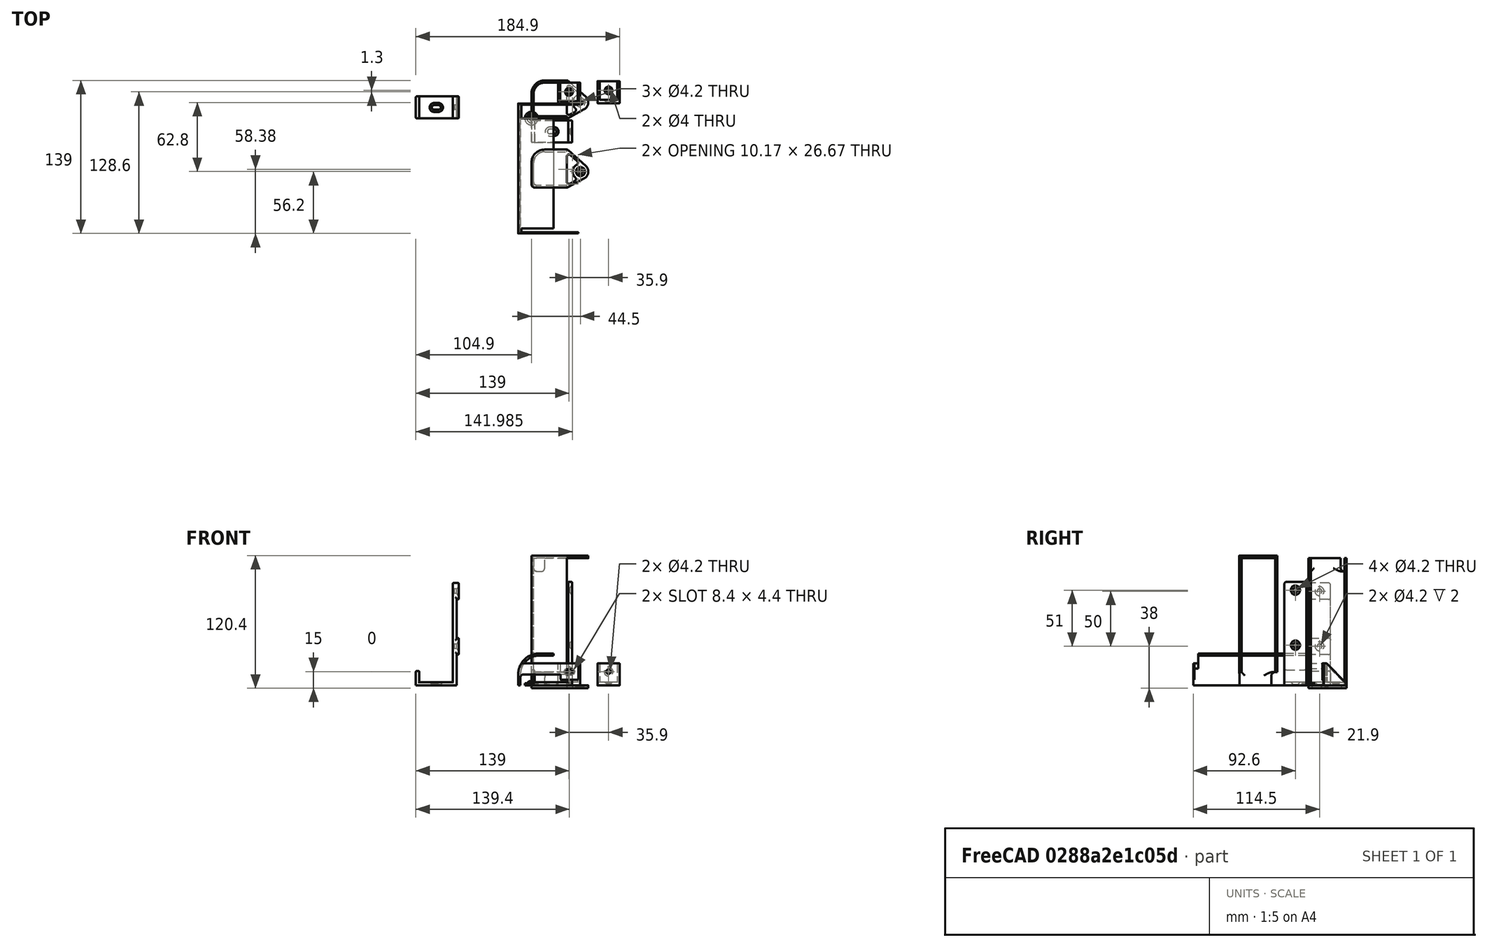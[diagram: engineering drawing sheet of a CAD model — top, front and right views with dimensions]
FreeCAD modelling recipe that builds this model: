
FCSTD DOCUMENT  (FreeCAD 1.0R39285 (Git))
Label: Mounts
License: All rights reserved
LicenseURL: https://en.wikipedia.org/wiki/All_rights_reserved
objects: Sketcher::SketchObject×38, PartDesign::Pad×19, PartDesign::Hole×10, PartDesign::Pocket×8, PartDesign::Body×8, Mesh::Feature×8, PartDesign::Fillet×3, PartDesign::Chamfer×2, PartDesign::Plane×1, PartDesign::Revolution×1
note: 214 computed .brp shape members not serialized (recipe doc carries the construction recipe); baked Part::Feature solids carry a one-line shape summary decoded from their .brp

FEATURE [Sketcher::SketchObject] Sketch  label="Sk-Mounting Angle Base"
  ArcFitTolerance = 1e-06
  AttachmentSupport = -> [XZ_Plane]
  FullyConstrained = true
  MakeInternals = false
  MapMode = 5
  Placement = pos=(0,0,0) rot=(1,0,0;1.5708rad)
  sketch-geometry (19):
    g0: LineSegment StartX=0 StartY=19 StartZ=0 EndX=0 EndY=1 EndZ=0
    g1: LineSegment StartX=1 StartY=0 StartZ=0 EndX=19 EndY=0 EndZ=0
    g2: LineSegment StartX=20 StartY=1 StartZ=0 EndX=20 EndY=2 EndZ=0
    g3: LineSegment StartX=19.7071 StartY=2.70711 StartZ=0 EndX=2.70711 EndY=19.7071 EndZ=0
    g4: LineSegment StartX=2 StartY=20 StartZ=0 EndX=1 EndY=20 EndZ=0
    g5: ArcOfCircle CenterX=1 CenterY=19 CenterZ=0 NormalX=0 NormalY=0 NormalZ=1 AngleXU=0 Radius=1 StartAngle=1.5708 EndAngle=3.14159
    g6: GeomPoint [constr] X=0 Y=20 Z=0
    g7: ArcOfCircle CenterX=2 CenterY=19 CenterZ=0 NormalX=0 NormalY=0 NormalZ=1 AngleXU=0 Radius=1 StartAngle=0.785398 EndAngle=1.5708
    g8: GeomPoint [constr] X=2.41421 Y=20 Z=0
    g9: ArcOfCircle CenterX=19 CenterY=2 CenterZ=0 NormalX=0 NormalY=0 NormalZ=1 AngleXU=0 Radius=1 StartAngle=1e-16 EndAngle=0.785398
    g10: GeomPoint [constr] X=20 Y=2.41421 Z=0
    g11: ArcOfCircle CenterX=19 CenterY=1 CenterZ=0 NormalX=0 NormalY=0 NormalZ=1 AngleXU=0 Radius=1 StartAngle=4.71239 EndAngle=6.28319
    g12: GeomPoint [constr] X=20 Y=0 Z=0
    g13: ArcOfCircle CenterX=1 CenterY=1 CenterZ=0 NormalX=0 NormalY=0 NormalZ=1 AngleXU=0 Radius=1 StartAngle=3.14159 EndAngle=4.71239
    g14: GeomPoint [constr] X=0 Y=0 Z=0
    g15: ArcOfCircle [constr] CenterX=2 CenterY=19 CenterZ=0 NormalX=0 NormalY=0 NormalZ=1 AngleXU=0 Radius=1 StartAngle=-1.8e-15 EndAngle=1.5708
    g16: LineSegment [constr] StartX=2 StartY=19 StartZ=0 EndX=3 EndY=19 EndZ=0
    g17: ArcOfCircle [constr] CenterX=19 CenterY=2 CenterZ=0 NormalX=0 NormalY=0 NormalZ=1 AngleXU=0 Radius=1 StartAngle=0 EndAngle=1.5708
    g18: LineSegment [constr] StartX=19 StartY=3 StartZ=0 EndX=19 EndY=2 EndZ=0
  constraints (44):
    c: Coincident(g14,g-1)
    c: Horizontal(g1)
    c: Vertical(g2)
    c: Vertical(g0)
    c: Horizontal(g4)
    c: DistanceY(g14,g6) = 20
    c: DistanceX(g14,g12) = 20
    c: PointOnObject(g6,g0)
    c: PointOnObject(g6,g4)
    c: Tangent(g0,g5) = -1.5708
    c: Tangent(g4,g5) = -1.5708
    c: PointOnObject(g8,g4)
    c: PointOnObject(g8,g3)
    c: Tangent(g4,g7) = -1.5708
    c: Tangent(g3,g7) = -1.5708
    c: PointOnObject(g10,g3)
    c: PointOnObject(g10,g2)
    c: Tangent(g3,g9) = -1.5708
    c: Tangent(g2,g9) = -1.5708
    c: PointOnObject(g12,g2)
    c: PointOnObject(g12,g1)
    c: Tangent(g2,g11) = -1.5708
    c: Tangent(g1,g11) = -1.5708
    c: PointOnObject(g14,g1)
    c: PointOnObject(g14,g0)
    c: Tangent(g1,g13) = -1.5708
    c: Tangent(g0,g13) = -1.5708
    c: Equal(g5,g7)
    c: Equal(g7,g9)
    c: Equal(g9,g11)
    c: Equal(g11,g13)
    c: Radius(g5) = 1
    c: Equal(g4,g2)
    c: Coincident(g15,g7)
    c: Coincident(g15,g4)
    c: Coincident(g16,g7)
    c: Coincident(g16,g15)
    c: Horizontal(g16)
    c: DistanceX(g0,g15) = 3
    c: Coincident(g17,g9)
    c: Coincident(g17,g2)
    c: Coincident(g18,g17)
    c: Coincident(g18,g9)
    c: Vertical(g18)
FEATURE [PartDesign::Pad] Pad  label="P-Mounting Angle Base"
  Direction = (0,-1,2e-16)
  Length = 20
  Length2 = 10
  Placement = pos=(0,0,0) rot=(1,0,0;1.5708rad)
  Profile = -> Sketch
  ReferenceAxis = -> Sketch [N_Axis]
  Refine = true
  Suppressed = false
  Type = 0
FEATURE [Sketcher::SketchObject] Sketch001  label="Sk-Mounting Angle Pocket"
  ArcFitTolerance = 1e-06
  AttachmentOffset = pos=(0,0,-2) rot=(0,0,1;0rad)
  AttachmentSupport = -> [Pad]
  ExternalGeometry = -> [Pad]
  FullyConstrained = true
  MakeInternals = false
  MapMode = 5
  Placement = pos=(0,-18,-4e-16) rot=(1,0,0;1.5708rad)
  sketch-geometry (20):
    g0: LineSegment StartX=3 StartY=19 StartZ=0 EndX=3 EndY=4 EndZ=0
    g1: LineSegment StartX=4 StartY=3 StartZ=0 EndX=19 EndY=3 EndZ=0
    g2: ArcOfCircle CenterX=4 CenterY=4 CenterZ=0 NormalX=0 NormalY=0 NormalZ=1 AngleXU=0 Radius=1 StartAngle=3.14159 EndAngle=4.71239
    g3: GeomPoint [constr] X=3 Y=3 Z=0
    g4: LineSegment [constr] StartX=2.7e-15 StartY=19 StartZ=0 EndX=2.7e-15 EndY=1 EndZ=0
    g5: LineSegment [constr] StartX=1 StartY=20 StartZ=0 EndX=2 EndY=20 EndZ=0
    g6: LineSegment [constr] StartX=1 StartY=2.75e-14 StartZ=0 EndX=19 EndY=2.75e-14 EndZ=0
    g7: LineSegment [constr] StartX=20 StartY=1 StartZ=0 EndX=20 EndY=2 EndZ=0
    g8: ArcOfCircle [constr] CenterX=1 CenterY=19 CenterZ=0 NormalX=0 NormalY=0 NormalZ=1 AngleXU=0 Radius=1 StartAngle=1.5708 EndAngle=3.14159
    g9: GeomPoint [constr] X=0 Y=20 Z=0
    g10: ArcOfCircle CenterX=2 CenterY=19 CenterZ=0 NormalX=0 NormalY=0 NormalZ=1 AngleXU=0 Radius=1 StartAngle=-3.189e-13 EndAngle=1.5708
    g11: GeomPoint [constr] X=3 Y=20 Z=0
    g12: ArcOfCircle [constr] CenterX=1 CenterY=1 CenterZ=0 NormalX=0 NormalY=0 NormalZ=1 AngleXU=0 Radius=1 StartAngle=3.14159 EndAngle=4.71239
    g13: GeomPoint [constr] X=0 Y=4.4e-15 Z=0
    g14: ArcOfCircle CenterX=19 CenterY=2 CenterZ=0 NormalX=0 NormalY=0 NormalZ=1 AngleXU=0 Radius=1 StartAngle=-1.643e-13 EndAngle=1.5708
    g15: GeomPoint [constr] X=20 Y=3 Z=0
    g16: ArcOfCircle [constr] CenterX=19 CenterY=1 CenterZ=0 NormalX=0 NormalY=0 NormalZ=1 AngleXU=0 Radius=1 StartAngle=4.71239 EndAngle=6.28319
    g17: GeomPoint [constr] X=20 Y=4.4e-15 Z=0
    g18: LineSegment StartX=2 StartY=20 StartZ=0 EndX=20 EndY=20 EndZ=0
    g19: LineSegment StartX=20 StartY=20 StartZ=0 EndX=20 EndY=2 EndZ=0
  constraints (43):
    c: Vertical(g0)
    c: Horizontal(g1)
    c: PointOnObject(g3,g0)
    c: PointOnObject(g3,g1)
    c: Tangent(g0,g2) = -1.5708
    c: Tangent(g1,g2) = -1.5708
    c: Horizontal(g5)
    c: Vertical(g4)
    c: Horizontal(g6)
    c: Vertical(g7)
    c: PointOnObject(g9,g4)
    c: PointOnObject(g9,g5)
    c: Tangent(g4,g8) = -1.5708
    c: Tangent(g5,g8) = 1.5708
    c: PointOnObject(g11,g5)
    c: PointOnObject(g11,g0)
    c: Tangent(g5,g10) = 1.5708
    c: Tangent(g0,g10) = 1.5708
    c: PointOnObject(g13,g4)
    c: PointOnObject(g13,g6)
    c: Tangent(g4,g12) = -1.5708
    c: Tangent(g6,g12) = -1.5708
    c: PointOnObject(g15,g1)
    c: PointOnObject(g15,g7)
    c: Tangent(g1,g14) = 1.5708
    c: Tangent(g7,g14) = -1.5708
    c: PointOnObject(g17,g6)
    c: PointOnObject(g17,g7)
    c: Tangent(g6,g16) = -1.5708
    c: Tangent(g7,g16) = -1.5708
    c: Equal(g10,g2)
    c: Equal(g2,g14)
    c: Equal(g16,g12)
    c: Equal(g8,g-4)
    c: Coincident(g4,g-4)
    c: Coincident(g10,g-3)
    c: Coincident(g6,g-5)
    c: Coincident(g14,g-6)
    c: Coincident(g18,g5)
    c: Horizontal(g18)
    c: Coincident(g19,g18)
    c: Coincident(g19,g7)
    c: Vertical(g19)
FEATURE [PartDesign::Pocket] Pocket  label="P- Mounting Angle Shape"
  BaseFeature = -> Pad
  Direction = (0,1,-2e-16)
  Length = 16
  Length2 = 5
  Placement = pos=(0,0,0) rot=(1,0,0;1.5708rad)
  Profile = -> Sketch001
  ReferenceAxis = -> Sketch001 [N_Axis]
  Refine = true
  Suppressed = false
  Type = 0
FEATURE [Sketcher::SketchObject] Sketch002  label="Sk-Mounting Angle Screwhole Bottom"
  ArcFitTolerance = 1e-06
  AttachmentSupport = -> [Pocket]
  ExternalGeometry = -> [Pocket]
  FullyConstrained = true
  MakeInternals = false
  MapMode = 5
  Placement = pos=(0,1.3e-15,3) rot=(0,0,1;3.14159rad)
  sketch-geometry (2):
    g0: Circle CenterX=-11.5 CenterY=10 CenterZ=0 NormalX=0 NormalY=0 NormalZ=1 AngleXU=0 Radius=2
    g1: LineSegment [constr] StartX=-4 StartY=10 StartZ=0 EndX=-19 EndY=10 EndZ=0
  constraints (4):
    c: Diameter(g0) = 4
    c: Symmetric(g-4,g-4,g1)
    c: Symmetric(g-3,g-3,g1)
    c: Symmetric(g1,g1,g0)
FEATURE [PartDesign::Hole] Hole  label="P-Mounting Angle Screwhole Bottom"
  BaseFeature = -> Pocket
  CustomThreadClearance = 0
  Depth = 69.9749
  DepthType = 1
  Diameter = 4
  DrillForDepth = false
  DrillPoint = 1
  DrillPointAngle = 118
  HoleCutCountersinkAngle = 90
  HoleCutCustomValues = false
  HoleCutDepth = 0
  HoleCutDiameter = 7
  HoleCutType = 2
  ModelThread = false
  Placement = pos=(0,0,0) rot=(1,0,0;1.5708rad)
  Profile = -> Sketch002
  Refine = true
  Suppressed = false
  Tapered = false
  TaperedAngle = 90
  ThreadClass = 0
  ThreadDepth = 69.9749
  ThreadDepthType = 0
  ThreadDirection = 0
  ThreadFit = 0
  ThreadSize = 0
  ThreadType = 0
  Threaded = false
  UseCustomThreadClearance = false
FEATURE [Sketcher::SketchObject] Sketch003  label="Sk-Mounting Angle Screwhole Side"
  ArcFitTolerance = 1e-06
  AttachmentSupport = -> [Hole]
  ExternalGeometry = -> [Hole]
  FullyConstrained = true
  MakeInternals = false
  MapMode = 5
  Placement = pos=(3,0,0) rot=(0.707107,0,0.707107;3.14159rad)
  sketch-geometry (2):
    g0: LineSegment [constr] StartX=1.8e-15 StartY=10 StartZ=0 EndX=12.5 EndY=10 EndZ=0
    g1: Circle CenterX=12.5 CenterY=10 CenterZ=0 NormalX=0 NormalY=0 NormalZ=1 AngleXU=0 Radius=2.2
  constraints (5):
    c: Symmetric(g-3,g-3,g0)
    c: Horizontal(g0)
    c: DistanceX(g0,g0) = 12.5
    c: Diameter(g1) = 4.4
    c: Coincident(g1,g0)
FEATURE [PartDesign::Hole] Hole001  label="P-Mounting Angle complete"
  BaseFeature = -> Hole
  CustomThreadClearance = 0
  Depth = 25
  DepthType = 0
  Diameter = 4.2
  DrillForDepth = false
  DrillPoint = 1
  DrillPointAngle = 118
  HoleCutCountersinkAngle = 90
  HoleCutCustomValues = false
  HoleCutDepth = 0
  HoleCutDiameter = 8.1
  HoleCutType = 2
  ModelThread = false
  Placement = pos=(0,0,0) rot=(1,0,0;1.5708rad)
  Profile = -> Sketch003
  Refine = true
  Suppressed = false
  Tapered = false
  TaperedAngle = 90
  ThreadClass = 0
  ThreadDepth = 25
  ThreadDepthType = 0
  ThreadDirection = 0
  ThreadFit = 0
  ThreadSize = 0
  ThreadType = 0
  Threaded = false
  UseCustomThreadClearance = false
FEATURE [PartDesign::Body] Body  label="B-Power Supply Mounting Angle - Flat"
  AllowCompound = false
  Group = -> [Sketch,Pad,Sketch001,Pocket,Sketch002,Hole,Sketch003,Hole001]
  Origin = -> Origin
  Placement = pos=(60,13.9,0) rot=(0,0,1;1.5708rad)
  Tip = -> Hole001
FEATURE [Sketcher::SketchObject] Sketch004  label="Sk-Mounting Angle Bracket Base"
  ArcFitTolerance = 1e-06
  AttachmentSupport = -> [XZ_Plane001]
  FullyConstrained = true
  MakeInternals = false
  MapMode = 5
  Placement = pos=(0,0,0) rot=(1,0,0;1.5708rad)
  sketch-geometry (20):
    g0: LineSegment [constr] StartX=0 StartY=19 StartZ=0 EndX=0 EndY=1 EndZ=0
    g1: LineSegment StartX=1 StartY=0 StartZ=0 EndX=19 EndY=0 EndZ=0
    g2: LineSegment StartX=20 StartY=1 StartZ=0 EndX=20 EndY=2 EndZ=0
    g3: LineSegment StartX=19.7071 StartY=2.70711 StartZ=0 EndX=2.70711 EndY=19.7071 EndZ=0
    g4: LineSegment StartX=2 StartY=20 StartZ=0 EndX=1 EndY=20 EndZ=0
    g5: ArcOfCircle [constr] CenterX=1 CenterY=19 CenterZ=0 NormalX=0 NormalY=0 NormalZ=1 AngleXU=0 Radius=1 StartAngle=1.5708 EndAngle=3.14159
    g6: GeomPoint [constr] X=0 Y=20 Z=0
    g7: ArcOfCircle CenterX=2 CenterY=19 CenterZ=0 NormalX=0 NormalY=0 NormalZ=1 AngleXU=0 Radius=1 StartAngle=0.785398 EndAngle=1.5708
    g8: GeomPoint [constr] X=2.41421 Y=20 Z=0
    g9: ArcOfCircle CenterX=19 CenterY=2 CenterZ=0 NormalX=0 NormalY=0 NormalZ=1 AngleXU=0 Radius=1 StartAngle=1e-16 EndAngle=0.785398
    g10: GeomPoint [constr] X=20 Y=2.41421 Z=0
    g11: ArcOfCircle CenterX=19 CenterY=1 CenterZ=0 NormalX=0 NormalY=0 NormalZ=1 AngleXU=0 Radius=1 StartAngle=4.71239 EndAngle=6.28319
    g12: GeomPoint [constr] X=20 Y=0 Z=0
    g13: ArcOfCircle [constr] CenterX=1 CenterY=1 CenterZ=0 NormalX=0 NormalY=0 NormalZ=1 AngleXU=0 Radius=1 StartAngle=3.14159 EndAngle=4.71239
    g14: GeomPoint [constr] X=0 Y=0 Z=0
    g15: ArcOfCircle [constr] CenterX=2 CenterY=19 CenterZ=0 NormalX=0 NormalY=0 NormalZ=1 AngleXU=0 Radius=1 StartAngle=-1.8e-15 EndAngle=1.5708
    g16: LineSegment [constr] StartX=2 StartY=19 StartZ=0 EndX=3 EndY=19 EndZ=0
    g17: ArcOfCircle [constr] CenterX=19 CenterY=2 CenterZ=0 NormalX=0 NormalY=0 NormalZ=1 AngleXU=0 Radius=1 StartAngle=0 EndAngle=1.5708
    g18: LineSegment [constr] StartX=19 StartY=3 StartZ=0 EndX=19 EndY=2 EndZ=0
    g19: LineSegment StartX=1 StartY=20 StartZ=0 EndX=1 EndY=0 EndZ=0
  constraints (46):
    c: Coincident(g14,g-1)
    c: Horizontal(g1)
    c: Vertical(g2)
    c: Vertical(g0)
    c: Horizontal(g4)
    c: DistanceY(g14,g6) = 20
    c: DistanceX(g14,g12) = 20
    c: PointOnObject(g6,g0)
    c: PointOnObject(g6,g4)
    c: Tangent(g0,g5) = -1.5708
    c: Tangent(g4,g5) = -1.5708
    c: PointOnObject(g8,g4)
    c: PointOnObject(g8,g3)
    c: Tangent(g4,g7) = -1.5708
    c: Tangent(g3,g7) = -1.5708
    c: PointOnObject(g10,g3)
    c: PointOnObject(g10,g2)
    c: Tangent(g3,g9) = -1.5708
    c: Tangent(g2,g9) = -1.5708
    c: PointOnObject(g12,g2)
    c: PointOnObject(g12,g1)
    c: Tangent(g2,g11) = -1.5708
    c: Tangent(g1,g11) = -1.5708
    c: PointOnObject(g14,g1)
    c: PointOnObject(g14,g0)
    c: Tangent(g1,g13) = -1.5708
    c: Tangent(g0,g13) = -1.5708
    c: Equal(g5,g7)
    c: Equal(g7,g9)
    c: Equal(g9,g11)
    c: Equal(g11,g13)
    c: Radius(g5) = 1
    c: Equal(g4,g2)
    c: Coincident(g15,g7)
    c: Coincident(g15,g4)
    c: Coincident(g16,g7)
    c: Coincident(g16,g15)
    c: Horizontal(g16)
    c: DistanceX(g0,g15) = 3
    c: Coincident(g17,g9)
    c: Coincident(g17,g2)
    c: Coincident(g18,g17)
    c: Coincident(g18,g9)
    c: Vertical(g18)
    c: Coincident(g19,g4)
    c: Coincident(g19,g1)
FEATURE [PartDesign::Pad] Pad001  label="P-Mounting Angle Bracket Base"
  Direction = (0,-1,2e-16)
  Length = 20
  Length2 = 10
  Placement = pos=(0,0,0) rot=(1,0,0;1.5708rad)
  Profile = -> Sketch004
  ReferenceAxis = -> Sketch004 [N_Axis]
  Refine = true
  Suppressed = false
  Type = 0
FEATURE [Sketcher::SketchObject] Sketch005  label="Sk-Mounting Angle Bracket Pocket"
  ArcFitTolerance = 1e-06
  AttachmentOffset = pos=(0,0,-2) rot=(0,0,1;0rad)
  AttachmentSupport = -> [Pad001]
  ExternalGeometry = -> [Pad001]
  FullyConstrained = true
  MakeInternals = false
  MapMode = 5
  Placement = pos=(0,-18,-4e-16) rot=(1,0,0;1.5708rad)
  sketch-geometry (8):
    g0: LineSegment StartX=3 StartY=19 StartZ=0 EndX=3 EndY=4 EndZ=0
    g1: LineSegment StartX=4 StartY=3 StartZ=0 EndX=19 EndY=3 EndZ=0
    g2: ArcOfCircle CenterX=4 CenterY=4 CenterZ=0 NormalX=0 NormalY=0 NormalZ=1 AngleXU=0 Radius=1 StartAngle=3.14159 EndAngle=4.71239
    g3: GeomPoint [constr] X=3 Y=3 Z=0
    g4: ArcOfCircle CenterX=2 CenterY=19 CenterZ=0 NormalX=0 NormalY=0 NormalZ=1 AngleXU=0 Radius=1 StartAngle=1.5e-15 EndAngle=1.5708
    g5: ArcOfCircle CenterX=19 CenterY=2 CenterZ=0 NormalX=0 NormalY=0 NormalZ=1 AngleXU=0 Radius=1 StartAngle=0 EndAngle=1.5708
    g6: LineSegment StartX=2 StartY=20 StartZ=0 EndX=20 EndY=20 EndZ=0
    g7: LineSegment StartX=20 StartY=20 StartZ=0 EndX=20 EndY=2 EndZ=0
  constraints (18):
    c: Vertical(g0)
    c: Horizontal(g1)
    c: PointOnObject(g3,g0)
    c: PointOnObject(g3,g1)
    c: Tangent(g0,g2) = -1.5708
    c: Tangent(g1,g2) = -1.5708
    c: Tangent(g0,g4) = 1.5708
    c: Tangent(g1,g5) = 1.5708
    c: Equal(g4,g2)
    c: Equal(g2,g5)
    c: Horizontal(g6)
    c: Coincident(g7,g6)
    c: Vertical(g7)
    c: Coincident(g5,g-4)
    c: PointOnObject(g-4,g5)
    c: Tangent(g7,g5) = 1.5708
    c: Tangent(g6,g4) = 1.5708
    c: Coincident(g4,g-3)
FEATURE [PartDesign::Pocket] Pocket001  label="P- Mounting Angle Bracket Shape"
  BaseFeature = -> Pad001
  Direction = (0,1,-2e-16)
  Length = 16
  Length2 = 5
  Placement = pos=(0,0,0) rot=(1,0,0;1.5708rad)
  Profile = -> Sketch005
  ReferenceAxis = -> Sketch005 [N_Axis]
  Refine = true
  Suppressed = false
  Type = 0
FEATURE [Sketcher::SketchObject] Sketch006  label="Sk-Mounting Angle Bracket Screwhole Bottom"
  ArcFitTolerance = 1e-06
  AttachmentSupport = -> [Pocket001]
  FullyConstrained = true
  MakeInternals = false
  MapMode = 5
  Placement = pos=(0,1.3e-15,3) rot=(0,0,1;3.14159rad)
  sketch-geometry (2):
    g0: Circle CenterX=-11.5 CenterY=10 CenterZ=0 NormalX=0 NormalY=0 NormalZ=1 AngleXU=0 Radius=2
    g1: LineSegment [constr] StartX=-4 StartY=10 StartZ=0 EndX=-19 EndY=10 EndZ=0
  constraints (4):
    c: Diameter(g0) = 4
    c: Symmetric(g-4,g-4,g1)
    c: Symmetric(g-3,g-3,g1)
    c: Symmetric(g1,g1,g0)
FEATURE [PartDesign::Hole] Hole002  label="P-Mounting Angle Bracket Screwhole Bottom"
  BaseFeature = -> Pocket001
  CustomThreadClearance = 0
  Depth = 69.9749
  DepthType = 1
  Diameter = 4
  DrillForDepth = false
  DrillPoint = 1
  DrillPointAngle = 118
  HoleCutCountersinkAngle = 90
  HoleCutCustomValues = false
  HoleCutDepth = 0
  HoleCutDiameter = 7
  HoleCutType = 2
  ModelThread = false
  Placement = pos=(0,0,0) rot=(1,0,0;1.5708rad)
  Profile = -> Sketch006
  Refine = true
  Suppressed = false
  Tapered = false
  TaperedAngle = 90
  ThreadClass = 0
  ThreadDepth = 69.9749
  ThreadDepthType = 0
  ThreadDirection = 0
  ThreadFit = 0
  ThreadSize = 0
  ThreadType = 0
  Threaded = false
  UseCustomThreadClearance = false
FEATURE [Sketcher::SketchObject] Sketch007  label="Sk-Mounting Angle Bracket Screwhole Side"
  ArcFitTolerance = 1e-06
  AttachmentSupport = -> [Hole002]
  ExternalGeometry = -> [Hole002]
  FullyConstrained = true
  MakeInternals = false
  MapMode = 5
  Placement = pos=(3,0,0) rot=(0.707107,0,0.707107;3.14159rad)
  sketch-geometry (2):
    g0: LineSegment [constr] StartX=5.8e-15 StartY=10 StartZ=0 EndX=12.5 EndY=10 EndZ=0
    g1: Circle CenterX=12.5 CenterY=10 CenterZ=0 NormalX=0 NormalY=0 NormalZ=1 AngleXU=0 Radius=2.2
  constraints (5):
    c: Horizontal(g0)
    c: DistanceX(g0,g0) = 12.5
    c: Diameter(g1) = 4.4
    c: Coincident(g1,g0)
    c: Symmetric(g-3,g-3,g0)
FEATURE [PartDesign::Hole] Hole003  label="P-Mounting Angle Bracket complete"
  BaseFeature = -> Hole002
  CustomThreadClearance = 0
  Depth = 25
  DepthType = 0
  Diameter = 4.2
  DrillForDepth = false
  DrillPoint = 1
  DrillPointAngle = 118
  HoleCutCountersinkAngle = 90
  HoleCutCustomValues = false
  HoleCutDepth = 0
  HoleCutDiameter = 8.1
  HoleCutType = 2
  ModelThread = false
  Placement = pos=(0,0,0) rot=(1,0,0;1.5708rad)
  Profile = -> Sketch007
  Refine = true
  Suppressed = false
  Tapered = false
  TaperedAngle = 90
  ThreadClass = 0
  ThreadDepth = 25
  ThreadDepthType = 0
  ThreadDirection = 0
  ThreadFit = 0
  ThreadSize = 0
  ThreadType = 0
  Threaded = false
  UseCustomThreadClearance = false
FEATURE [PartDesign::Body] Body001  label="B-Power Supply Mounting Angle for Bracket - Flat"
  AllowCompound = false
  Group = -> [Sketch004,Pad001,Sketch005,Pocket001,Sketch006,Hole002,Sketch007,Hole003]
  Origin = -> Origin001
  Placement = pos=(24.1,12.6,0) rot=(0,0,1;1.5708rad)
  Tip = -> Hole003
FEATURE [Sketcher::SketchObject] Sketch008  label="Sk-Bracket Shield"
  ArcFitTolerance = 1e-06
  AttachmentSupport = -> [XZ_Plane002]
  FullyConstrained = true
  MakeInternals = false
  MapMode = 5
  Placement = pos=(0,0,0) rot=(1,0,0;1.5708rad)
  sketch-geometry (11):
    g0: LineSegment StartX=20 StartY=29 StartZ=0 EndX=7 EndY=29 EndZ=0
    g1: LineSegment StartX=-12 StartY=10 StartZ=0 EndX=-12 EndY=0 EndZ=0
    g2: LineSegment StartX=-12 StartY=0 StartZ=0 EndX=-10 EndY=0 EndZ=0
    g3: LineSegment StartX=-10 StartY=0 StartZ=0 EndX=-10 EndY=10 EndZ=0
    g4: LineSegment StartX=7 StartY=27 StartZ=0 EndX=20 EndY=27 EndZ=0
    g5: LineSegment StartX=20 StartY=27 StartZ=0 EndX=20 EndY=29 EndZ=0
    g6: ArcOfCircle CenterX=7 CenterY=10 CenterZ=0 NormalX=0 NormalY=0 NormalZ=1 AngleXU=0 Radius=19 StartAngle=1.5708 EndAngle=3.14159
    g7: GeomPoint [constr] X=-12 Y=29 Z=0
    g8: ArcOfCircle CenterX=7 CenterY=10 CenterZ=0 NormalX=0 NormalY=0 NormalZ=1 AngleXU=0 Radius=17 StartAngle=1.5708 EndAngle=3.14159
    g9: GeomPoint [constr] X=-10 Y=27 Z=0
    g10: LineSegment [constr] StartX=-10 StartY=0 StartZ=0 EndX=0 EndY=0 EndZ=0
  constraints (28):
    c: Horizontal(g0)
    c: Coincident(g1,g2)
    c: Horizontal(g2)
    c: Coincident(g2,g3)
    c: Horizontal(g4)
    c: Coincident(g4,g5)
    c: Coincident(g5,g0)
    c: Vertical(g5)
    c: Vertical(g1)
    c: Vertical(g3)
    c: PointOnObject(g7,g0)
    c: PointOnObject(g7,g1)
    c: Tangent(g0,g6) = -1.5708
    c: Tangent(g1,g6) = -1.5708
    c: PointOnObject(g9,g4)
    c: PointOnObject(g9,g3)
    c: Tangent(g4,g8) = 1.5708
    c: Tangent(g3,g8) = 1.5708
    c: Coincident(g10,g2)
    c: Coincident(g10,g-1)
    c: Horizontal(g10)
    c: DistanceX(g10,g10) = 10
    c: DistanceX(g2,g2) = 2
    c: Coincident(g6,g8)
    c: DistanceY(g1,g0) = 29
    c: DistanceX(g10,g4) = 20
    c: Radius(g8) = 17
    c: DistanceY(g1,g1) = 10
FEATURE [PartDesign::Pad] Pad002  label="P-Bracket Shield"
  Direction = (0,-1,2e-16)
  Length = 100
  Length2 = 10
  Placement = pos=(0,0,0) rot=(1,0,0;1.5708rad)
  Profile = -> Sketch008
  ReferenceAxis = -> Sketch008 [N_Axis]
  Refine = true
  Suppressed = false
  Type = 0
FEATURE [Sketcher::SketchObject] Sketch009  label="Sk-Bracket Dist front"
  ArcFitTolerance = 1e-06
  AttachmentSupport = -> [Pad002]
  ExternalGeometry = -> [Pad002]
  FullyConstrained = true
  MakeInternals = false
  MapMode = 5
  Placement = pos=(0,-100,0) rot=(1,0,0;1.5708rad)
  sketch-geometry (6):
    g0: ArcOfCircle CenterX=7 CenterY=10 CenterZ=0 NormalX=0 NormalY=0 NormalZ=1 AngleXU=0 Radius=17 StartAngle=2.82507 EndAngle=3.14159
    g1: ArcOfCircle CenterX=7 CenterY=10 CenterZ=0 NormalX=0 NormalY=0 NormalZ=1 AngleXU=0 Radius=19 StartAngle=2.58733 EndAngle=3.14159
    g2: LineSegment StartX=-9.15549 StartY=20 StartZ=0 EndX=-9.15549 EndY=15.2915 EndZ=0
    g3: LineSegment StartX=-10 StartY=10 StartZ=0 EndX=-10 EndY=2.31e-14 EndZ=0
    g4: LineSegment StartX=-10 StartY=2.31e-14 StartZ=0 EndX=-12 EndY=2.22e-14 EndZ=0
    g5: LineSegment StartX=-12 StartY=2.22e-14 StartZ=0 EndX=-12 EndY=10 EndZ=0
  constraints (15):
    c: Coincident(g0,g-3)
    c: Coincident(g1,g0)
    c: Coincident(g2,g1)
    c: Coincident(g2,g0)
    c: Vertical(g2)
    c: Tangent(g3,g0) = -1.5708
    c: Coincident(g3,g-4)
    c: Coincident(g4,g3)
    c: Coincident(g4,g-4)
    c: Coincident(g5,g4)
    c: Coincident(g5,g1)
    c: Vertical(g5)
    c: PointOnObject(g0,g-3)
    c: Equal(g3,g5)
    c: DistanceY(g4,g1) = 20
FEATURE [PartDesign::Pad] Pad003  label="P-Bracket Shield left dist"
  BaseFeature = -> Pad002
  Direction = (0,-1,2e-16)
  Length = 3.5
  Length2 = 10
  Placement = pos=(0,0,0) rot=(1,0,0;1.5708rad)
  Profile = -> Sketch009
  ReferenceAxis = -> Sketch009 [N_Axis]
  Refine = true
  Suppressed = false
  Type = 0
FEATURE [Sketcher::SketchObject] Sketch010  label="Sk-Bracket Dist rear"
  ArcFitTolerance = 1e-06
  AttachmentSupport = -> [Pad003]
  ExternalGeometry = -> [Pad003]
  FullyConstrained = true
  MakeInternals = false
  MapMode = 5
  Placement = pos=(0,4.3e-15,0) rot=(-1,0,0;1.5708rad)
  sketch-geometry (6):
    g0: ArcOfCircle CenterX=7 CenterY=-10 CenterZ=0 NormalX=0 NormalY=0 NormalZ=1 AngleXU=0 Radius=17 StartAngle=3.14159 EndAngle=3.45812
    g1: ArcOfCircle CenterX=7 CenterY=-10 CenterZ=0 NormalX=0 NormalY=0 NormalZ=1 AngleXU=0 Radius=19 StartAngle=3.14159 EndAngle=3.69585
    g2: LineSegment StartX=-9.15549 StartY=-20 StartZ=0 EndX=-9.15549 EndY=-15.2915 EndZ=0
    g3: LineSegment StartX=-10 StartY=-10 StartZ=0 EndX=-10 EndY=0 EndZ=0
    g4: LineSegment StartX=-10 StartY=0 StartZ=0 EndX=-12 EndY=0 EndZ=0
    g5: LineSegment StartX=-12 StartY=0 StartZ=0 EndX=-12 EndY=-10 EndZ=0
  constraints (15):
    c: Coincident(g0,g-3)
    c: Coincident(g0,g-3)
    c: Coincident(g1,g0)
    c: Coincident(g2,g1)
    c: Coincident(g2,g0)
    c: Vertical(g2)
    c: Coincident(g3,g0)
    c: Coincident(g3,g-4)
    c: Coincident(g4,g3)
    c: Coincident(g4,g-4)
    c: Coincident(g5,g4)
    c: Coincident(g5,g1)
    c: Vertical(g5)
    c: PointOnObject(g0,g-5)
    c: Equal(g3,g5)
FEATURE [PartDesign::Pad] Pad004  label="P-Bracket Shield dists"
  BaseFeature = -> Pad003
  Direction = (0,1,2e-16)
  Length = 12.5
  Length2 = 10
  Placement = pos=(0,0,0) rot=(1,0,0;1.5708rad)
  Profile = -> Sketch010
  ReferenceAxis = -> Sketch010 [N_Axis]
  Refine = true
  Suppressed = false
  Type = 0
FEATURE [Sketcher::SketchObject] Sketch011  label="Sk-Bracket front mount"
  ArcFitTolerance = 1e-06
  AttachmentSupport = -> [Pad004]
  ExternalGeometry = -> [Pad004]
  FullyConstrained = true
  MakeInternals = false
  MapMode = 5
  Placement = pos=(0,-103.5,0) rot=(1,0,0;1.5708rad)
  sketch-geometry (33):
    g0: ArcOfCircle CenterX=7 CenterY=10 CenterZ=0 NormalX=0 NormalY=0 NormalZ=1 AngleXU=0 Radius=19 StartAngle=2.58733 EndAngle=3.14159
    g1: LineSegment StartX=-9.15549 StartY=20 StartZ=0 EndX=41.5 EndY=20 EndZ=0
    g2: LineSegment StartX=42.5 StartY=19 StartZ=0 EndX=42.5 EndY=6 EndZ=0
    g3: LineSegment StartX=26.5 StartY=6 StartZ=0 EndX=26.5 EndY=9 EndZ=0
    g4: LineSegment [constr] StartX=20 StartY=29 StartZ=0 EndX=2 EndY=29 EndZ=0
    g5: LineSegment [constr] StartX=2 StartY=29 StartZ=0 EndX=2 EndY=12.5 EndZ=0
    g6: LineSegment [constr] StartX=2 StartY=12.5 StartZ=0 EndX=2 EndY=0 EndZ=0
    g7: ArcOfCircle CenterX=32.5 CenterY=12.5 CenterZ=0 NormalX=0 NormalY=0 NormalZ=1 AngleXU=0 Radius=2.2 StartAngle=1.5708 EndAngle=4.71239
    g8: ArcOfCircle CenterX=36.5 CenterY=12.5 CenterZ=0 NormalX=0 NormalY=0 NormalZ=1 AngleXU=0 Radius=2.2 StartAngle=4.71239 EndAngle=7.85398
    g9: LineSegment StartX=32.5 StartY=14.7 StartZ=0 EndX=36.5 EndY=14.7 EndZ=0
    g10: LineSegment StartX=32.5 StartY=10.3 StartZ=0 EndX=36.5 EndY=10.3 EndZ=0
    g11: LineSegment [constr] StartX=2 StartY=12.5 StartZ=0 EndX=32.5 EndY=12.5 EndZ=0
    g12: LineSegment [constr] StartX=32.5 StartY=12.5 StartZ=0 EndX=34.5 EndY=12.5 EndZ=0
    g13: LineSegment [constr] StartX=34.5 StartY=12.5 StartZ=0 EndX=36.5 EndY=12.5 EndZ=0
    g14: LineSegment StartX=41.5 StartY=5 StartZ=0 EndX=34.5 EndY=5 EndZ=0
    g15: LineSegment StartX=34.5 StartY=5 StartZ=0 EndX=27.5 EndY=5 EndZ=0
    g16: LineSegment [constr] StartX=34.5 StartY=12.5 StartZ=0 EndX=34.5 EndY=5 EndZ=0
    g17: LineSegment [constr] StartX=34.5 StartY=12.5 StartZ=0 EndX=34.5 EndY=20 EndZ=0
    g18: LineSegment StartX=25.5 StartY=10 StartZ=0 EndX=-7 EndY=10 EndZ=0
    g19: LineSegment StartX=-12 StartY=10 StartZ=0 EndX=-12 EndY=0 EndZ=0
    g20: LineSegment StartX=-12 StartY=0 StartZ=0 EndX=-10 EndY=2.39e-14 EndZ=0
    g21: LineSegment StartX=-10 StartY=2.39e-14 StartZ=0 EndX=-10 EndY=7 EndZ=0
    g22: LineSegment [constr] StartX=-12 StartY=10 StartZ=0 EndX=-10 EndY=10 EndZ=0
    g23: ArcOfCircle CenterX=27.5 CenterY=6 CenterZ=0 NormalX=0 NormalY=0 NormalZ=1 AngleXU=0 Radius=1 StartAngle=3.14159 EndAngle=4.71239
    g24: GeomPoint [constr] X=26.5 Y=5 Z=0
    g25: ArcOfCircle CenterX=41.5 CenterY=6 CenterZ=0 NormalX=0 NormalY=0 NormalZ=1 AngleXU=0 Radius=1 StartAngle=4.71239 EndAngle=6.28319
    g26: GeomPoint [constr] X=42.5 Y=5 Z=0
    g27: ArcOfCircle CenterX=41.5 CenterY=19 CenterZ=0 NormalX=0 NormalY=0 NormalZ=1 AngleXU=0 Radius=1 StartAngle=0 EndAngle=1.5708
    g28: GeomPoint [constr] X=42.5 Y=20 Z=0
    g29: ArcOfCircle CenterX=25.5 CenterY=9 CenterZ=0 NormalX=0 NormalY=0 NormalZ=1 AngleXU=0 Radius=1 StartAngle=3e-16 EndAngle=1.5708
    g30: GeomPoint [constr] X=26.5 Y=10 Z=0
    g31: ArcOfCircle CenterX=-7 CenterY=7 CenterZ=0 NormalX=0 NormalY=0 NormalZ=1 AngleXU=0 Radius=3 StartAngle=1.5708 EndAngle=3.14159
    g32: GeomPoint [constr] X=-10 Y=10 Z=0
  constraints (80):
    c: Coincident(g0,g-3)
    c: Coincident(g0,g-3)
    c: Coincident(g1,g0)
    c: Horizontal(g1)
    c: Vertical(g2)
    c: Vertical(g3)
    c: PointOnObject(g-3,g1)
    c: Distance(g4) = 18
    c: Coincident(g4,g-4)
    c: Horizontal(g4)
    c: Coincident(g5,g4)
    c: Vertical(g5)
    c: Coincident(g11,g5)
    c: DistanceX(g11,g12) = 32.5
    c: Coincident(g6,g5)
    c: PointOnObject(g6,g-1)
    c: Vertical(g6)
    c: DistanceY(g6,g6) = 12.5
    c: Tangent(g7,g9) = 1.5708
    c: Tangent(g7,g10) = -1.5708
    c: Tangent(g8,g9) = 1.5708
    c: Tangent(g8,g10) = -1.5708
    c: Equal(g7,g8)
    c: Radius(g7) = 2.2
    c: Horizontal(g9)
    c: Coincident(g11,g12)
    c: Horizontal(g11)
    c: Horizontal(g12)
    c: Coincident(g11,g7)
    c: Coincident(g13,g12)
    c: Coincident(g13,g8)
    c: Equal(g13,g12)
    c: DistanceX(g10,g10) = 4
    c: Coincident(g14,g15)
    c: Horizontal(g14)
    c: Horizontal(g15)
    c: Coincident(g16,g12)
    c: Coincident(g16,g14)
    c: Vertical(g16)
    c: Coincident(g17,g12)
    c: PointOnObject(g17,g1)
    c: Vertical(g17)
    c: Equal(g17,g16)
    c: DistanceX(g24,g26) = 16
    c: Horizontal(g18)
    c: Coincident(g19,g0)
    c: Coincident(g19,g-5)
    c: Coincident(g20,g19)
    c: Coincident(g20,g-5)
    c: Coincident(g21,g20)
    c: Vertical(g21)
    c: Coincident(g22,g0)
    c: Coincident(g22,g32)
    c: Horizontal(g22)
    c: PointOnObject(g24,g3)
    c: PointOnObject(g24,g15)
    c: Tangent(g3,g23) = 1.5708
    c: Tangent(g15,g23) = 1.5708
    c: PointOnObject(g26,g2)
    c: PointOnObject(g26,g14)
    c: Tangent(g2,g25) = 1.5708
    c: Tangent(g14,g25) = 1.5708
    c: PointOnObject(g28,g1)
    c: PointOnObject(g28,g2)
    c: Tangent(g1,g27) = 1.5708
    c: Tangent(g2,g27) = 1.5708
    c: PointOnObject(g30,g18)
    c: PointOnObject(g30,g3)
    c: Tangent(g18,g29) = -1.5708
    c: Tangent(g3,g29) = -1.5708
    c: PointOnObject(g32,g21)
    c: PointOnObject(g32,g18)
    c: Tangent(g21,g31) = 1.5708
    c: Tangent(g18,g31) = -1.5708
    c: Equal(g29,g23)
    c: Equal(g23,g25)
    c: Equal(g25,g27)
    c: Radius(g27) = 1
    c: Radius(g31) = 3
    c: Equal(g15,g14)
FEATURE [PartDesign::Pad] Pad005  label="P-Bracket with front mount"
  BaseFeature = -> Pad004
  Direction = (0,-1,2e-16)
  Length = 1
  Length2 = 10
  Placement = pos=(0,0,0) rot=(1,0,0;1.5708rad)
  Profile = -> Sketch011
  ReferenceAxis = -> Sketch011 [N_Axis]
  Refine = true
  Suppressed = false
  Type = 0
FEATURE [Sketcher::SketchObject] Sketch012  label="Sk-Bracket rear mount"
  ArcFitTolerance = 1e-06
  AttachmentSupport = -> [Pad005]
  ExternalGeometry = -> [Pad005]
  FullyConstrained = false
  MakeInternals = false
  MapMode = 5
  Placement = pos=(0,12.5,2.8e-15) rot=(-1,0,0;1.5708rad)
  sketch-geometry (20):
    g0: LineSegment StartX=-12 StartY=0 StartZ=0 EndX=-10 EndY=0 EndZ=0
    g1: LineSegment StartX=-10 StartY=-7 StartZ=0 EndX=-10 EndY=0 EndZ=0
    g2: LineSegment StartX=-12 StartY=0 StartZ=0 EndX=-12 EndY=-10 EndZ=0
    g3: LineSegment StartX=-7 StartY=-10 StartZ=0 EndX=25.5 EndY=-10 EndZ=0
    g4: LineSegment StartX=26.5 StartY=-9 StartZ=0 EndX=26.5 EndY=-6 EndZ=0
    g5: LineSegment StartX=27.5 StartY=-5 StartZ=0 EndX=41.5 EndY=-5 EndZ=0
    g6: LineSegment StartX=42.5 StartY=-6 StartZ=0 EndX=42.5 EndY=-19 EndZ=0
    g7: LineSegment StartX=41.5 StartY=-20 StartZ=0 EndX=-9.15549 EndY=-20 EndZ=0
    g8: ArcOfCircle CenterX=7 CenterY=-10 CenterZ=0 NormalX=0 NormalY=0 NormalZ=1 AngleXU=0 Radius=19 StartAngle=3.14159 EndAngle=3.69585
    g9: ArcOfCircle CenterX=-7 CenterY=-7 CenterZ=0 NormalX=0 NormalY=0 NormalZ=1 AngleXU=0 Radius=3 StartAngle=3.14159 EndAngle=4.71239
    g10: ArcOfCircle CenterX=25.5 CenterY=-9 CenterZ=0 NormalX=0 NormalY=0 NormalZ=1 AngleXU=0 Radius=1 StartAngle=4.71239 EndAngle=6.28319
    g11: ArcOfCircle CenterX=27.5 CenterY=-6 CenterZ=0 NormalX=0 NormalY=0 NormalZ=1 AngleXU=0 Radius=1 StartAngle=1.5708 EndAngle=3.14159
    g12: ArcOfCircle CenterX=41.5 CenterY=-6 CenterZ=0 NormalX=0 NormalY=0 NormalZ=1 AngleXU=0 Radius=1 StartAngle=0 EndAngle=1.5708
    g13: GeomPoint [constr] X=42.5 Y=-5 Z=0
    g14: ArcOfCircle CenterX=41.5 CenterY=-19 CenterZ=0 NormalX=0 NormalY=0 NormalZ=1 AngleXU=0 Radius=1 StartAngle=4.71239 EndAngle=6.28319
    g15: GeomPoint [constr] X=42.5 Y=-20 Z=0
    g16: ArcOfCircle CenterX=32.5 CenterY=-12.5 CenterZ=0 NormalX=0 NormalY=0 NormalZ=1 AngleXU=0 Radius=2.2 StartAngle=1.5708 EndAngle=4.71239
    g17: ArcOfCircle CenterX=36.5 CenterY=-12.5 CenterZ=0 NormalX=0 NormalY=0 NormalZ=1 AngleXU=0 Radius=2.2 StartAngle=4.71239 EndAngle=7.85398
    g18: LineSegment StartX=32.5 StartY=-10.3 StartZ=0 EndX=36.5 EndY=-10.3 EndZ=0
    g19: LineSegment StartX=32.5 StartY=-14.7 StartZ=0 EndX=36.5 EndY=-14.7 EndZ=0
  constraints (43):
    c: Coincident(g0,g-3)
    c: Coincident(g0,g-3)
    c: Coincident(g1,g-6)
    c: Coincident(g1,g0)
    c: Coincident(g2,g0)
    c: Coincident(g2,g-4)
    c: Coincident(g3,g-6)
    c: Coincident(g3,g-7)
    c: Coincident(g4,g-7)
    c: Coincident(g4,g-8)
    c: Coincident(g5,g-8)
    c: Horizontal(g5)
    c: Vertical(g6)
    c: Coincident(g8,g-4)
    c: Coincident(g8,g2)
    c: Coincident(g8,g7)
    c: Coincident(g9,g-6)
    c: Coincident(g9,g1)
    c: Coincident(g9,g3)
    c: Coincident(g10,g-7)
    c: Coincident(g10,g3)
    c: Coincident(g11,g-8)
    c: Coincident(g11,g4)
    c: PointOnObject(g13,g5)
    c: PointOnObject(g13,g6)
    c: Tangent(g5,g12) = 1.5708
    c: Tangent(g6,g12) = 1.5708
    c: PointOnObject(g15,g6)
    c: PointOnObject(g15,g7)
    c: Tangent(g6,g14) = 1.5708
    c: Tangent(g7,g14) = 1.5708
    c: Coincident(g6,g-5)
    c: Coincident(g7,g-5)
    c: Equal(g11,g12)
    c: Tangent(g16,g18) = 1.5708
    c: Tangent(g16,g19) = -1.5708
    c: Tangent(g17,g18) = 1.5708
    c: Tangent(g17,g19) = -1.5708
    c: Equal(g16,g17)
    c: Equal(g17,g-10)
    c: Coincident(g16,g-9)
    c: Coincident(g17,g-10)
    c: Coincident(g5,g11)
FEATURE [PartDesign::Pad] Pad006
  BaseFeature = -> Pad005
  Direction = (0,1,2e-16)
  Length = 1
  Length2 = 10
  Placement = pos=(0,0,0) rot=(1,0,0;1.5708rad)
  Profile = -> Sketch012
  ReferenceAxis = -> Sketch012 [N_Axis]
  Refine = true
  Suppressed = false
  Type = 0
FEATURE [PartDesign::Body] Body002  label="B-Power Supply Bracket - Flat"
  AllowCompound = false
  Group = -> [Sketch008,Pad002,Sketch009,Pad003,Sketch010,Pad004,Sketch011,Pad005,Sketch012,Pad006]
  Origin = -> Origin002
  Tip = -> Pad006
FEATURE [Mesh::Feature] Mesh  label="M-Power Supply Mounting Angle - Flat"
FEATURE [Mesh::Feature] Mesh001  label="M-Power Supply Mounting Angle for Bracket - Flat"
FEATURE [Mesh::Feature] Mesh002  label="M-Power Supply Bracket - Flat"
FEATURE [Sketcher::SketchObject] Sketch013  label="Sk-PsMb-Base"
  ArcFitTolerance = 1e-06
  AttachmentSupport = -> [XY_Plane003]
  FullyConstrained = true
  MakeInternals = false
  MapMode = 5
  sketch-geometry (5):
    g0: LineSegment StartX=3 StartY=0 StartZ=0 EndX=33.5 EndY=0 EndZ=0
    g1: LineSegment StartX=33.5 StartY=0 StartZ=0 EndX=33.5 EndY=20 EndZ=0
    g2: LineSegment StartX=33.5 StartY=20 StartZ=0 EndX=3 EndY=20 EndZ=0
    g3: LineSegment StartX=3 StartY=20 StartZ=0 EndX=3 EndY=0 EndZ=0
    g4: LineSegment [constr] StartX=0 StartY=0 StartZ=0 EndX=3 EndY=0 EndZ=0
  constraints (14):
    c: Horizontal(g0)
    c: Horizontal(g2)
    c: Vertical(g1)
    c: Vertical(g3)
    c: Distance(g1,g3) = 30.5
    c: Distance(g0,g2) = 20
    c: Coincident(g0,g3)
    c: Coincident(g0,g1)
    c: Coincident(g1,g2)
    c: Coincident(g3,g2)
    c: Coincident(g4,g-1)
    c: Coincident(g4,g0)
    c: Horizontal(g4)
    c: DistanceX(g4,g4) = 3
FEATURE [PartDesign::Pad] Pad007  label="P-PsMb-Base"
  Direction = (0,0,1)
  Length = 3
  Length2 = 10
  Profile = -> Sketch013
  ReferenceAxis = -> Sketch013 [N_Axis]
  Refine = true
  Suppressed = false
  Type = 0
FEATURE [Sketcher::SketchObject] Sketch014  label="Sk-PsMb-Low"
  ArcFitTolerance = 1e-06
  AttachmentSupport = -> [Pad007]
  ExternalGeometry = -> [Pad007]
  FullyConstrained = true
  MakeInternals = false
  MapMode = 5
  Placement = pos=(3,0,0) rot=(0.57735,-0.57735,-0.57735;2.0944rad)
  sketch-geometry (8):
    g0: LineSegment StartX=-20 StartY=0 StartZ=0 EndX=0 EndY=0 EndZ=0
    g1: LineSegment StartX=-4e-16 StartY=0 StartZ=0 EndX=-4e-16 EndY=11 EndZ=0
    g2: LineSegment StartX=-2 StartY=13 StartZ=0 EndX=-18 EndY=13 EndZ=0
    g3: LineSegment StartX=-20 StartY=11 StartZ=0 EndX=-20 EndY=0 EndZ=0
    g4: ArcOfCircle CenterX=-18 CenterY=11 CenterZ=0 NormalX=0 NormalY=0 NormalZ=1 AngleXU=0 Radius=2 StartAngle=1.5708 EndAngle=3.14159
    g5: GeomPoint [constr] X=-20 Y=13 Z=0
    g6: ArcOfCircle CenterX=-2 CenterY=11 CenterZ=0 NormalX=0 NormalY=0 NormalZ=1 AngleXU=0 Radius=2 StartAngle=1e-16 EndAngle=1.5708
    g7: GeomPoint [constr] X=0 Y=13 Z=0
  constraints (18):
    c: Coincident(g0,g1)
    c: Coincident(g3,g0)
    c: Horizontal(g2)
    c: Vertical(g1)
    c: Vertical(g3)
    c: Coincident(g0,g-3)
    c: Coincident(g0,g-1)
    c: DistanceY(g3,g5) = 13
    c: PointOnObject(g5,g3)
    c: PointOnObject(g5,g2)
    c: Tangent(g3,g4) = -1.5708
    c: Tangent(g2,g4) = -1.5708
    c: PointOnObject(g7,g2)
    c: PointOnObject(g7,g1)
    c: Tangent(g2,g6) = -1.5708
    c: Tangent(g1,g6) = -1.5708
    c: Equal(g4,g6)
    c: Radius(g6) = 2
FEATURE [PartDesign::Pad] Pad008  label="P-PsMb-Rear-Low"
  BaseFeature = -> Pad007
  Direction = (-1,0,0)
  Length = 3
  Length2 = 10
  Profile = -> Sketch014
  ReferenceAxis = -> Sketch014 [N_Axis]
  Refine = true
  Suppressed = false
  Type = 0
FEATURE [Sketcher::SketchObject] Sketch015  label="Sk-PsMb-High"
  ArcFitTolerance = 1e-06
  AttachmentSupport = -> [Pad008]
  ExternalGeometry = -> [Pad008]
  FullyConstrained = true
  MakeInternals = false
  MapMode = 5
  Placement = pos=(33.5,0,0) rot=(0.57735,0.57735,0.57735;2.0944rad)
  sketch-geometry (8):
    g0: LineSegment StartX=20 StartY=0 StartZ=0 EndX=20 EndY=91 EndZ=0
    g1: LineSegment StartX=18 StartY=93 StartZ=0 EndX=2 EndY=93 EndZ=0
    g2: LineSegment StartX=0 StartY=91 StartZ=0 EndX=0 EndY=0 EndZ=0
    g3: LineSegment StartX=0 StartY=0 StartZ=0 EndX=20 EndY=0 EndZ=0
    g4: ArcOfCircle CenterX=2 CenterY=91 CenterZ=0 NormalX=0 NormalY=0 NormalZ=1 AngleXU=0 Radius=2 StartAngle=1.5708 EndAngle=3.14159
    g5: GeomPoint [constr] X=0 Y=93 Z=0
    g6: ArcOfCircle CenterX=18 CenterY=91 CenterZ=0 NormalX=0 NormalY=0 NormalZ=1 AngleXU=0 Radius=2 StartAngle=0 EndAngle=1.5708
    g7: GeomPoint [constr] X=20 Y=93 Z=0
  constraints (18):
    c: Coincident(g2,g3)
    c: Coincident(g3,g0)
    c: Vertical(g0)
    c: Vertical(g2)
    c: Horizontal(g1)
    c: Coincident(g0,g-3)
    c: Coincident(g-1,g2)
    c: PointOnObject(g5,g2)
    c: PointOnObject(g5,g1)
    c: Tangent(g2,g4) = -1.5708
    c: Tangent(g1,g4) = -1.5708
    c: PointOnObject(g7,g1)
    c: PointOnObject(g7,g0)
    c: Tangent(g1,g6) = -1.5708
    c: Tangent(g0,g6) = -1.5708
    c: Equal(g4,g6)
    c: Radius(g4) = 2
    c: DistanceY(g0,g1) = 93
FEATURE [PartDesign::Pad] Pad009  label="P-PsMb-raw"
  BaseFeature = -> Pad008
  Direction = (1,0,0)
  Length = 3.5
  Length2 = 10
  Profile = -> Sketch015
  ReferenceAxis = -> Sketch015 [N_Axis]
  Refine = true
  Suppressed = false
  Type = 0
FEATURE [Sketcher::SketchObject] Sketch016  label="Sk-PsMb-Ps-Screwholes"
  ArcFitTolerance = 1e-06
  AttachmentSupport = -> [Pad009]
  ExternalGeometry = -> [Pad009]
  FullyConstrained = true
  MakeInternals = false
  MapMode = 5
  Placement = pos=(37,0,0) rot=(0.57735,0.57735,0.57735;2.0944rad)
  sketch-geometry (5):
    g0: LineSegment [constr] StartX=10 StartY=3 StartZ=0 EndX=10 EndY=35.5 EndZ=0
    g1: LineSegment [constr] StartX=10 StartY=35.5 StartZ=0 EndX=10 EndY=85.5 EndZ=0
    g2: Circle CenterX=10 CenterY=35.5 CenterZ=0 NormalX=0 NormalY=0 NormalZ=1 AngleXU=0 Radius=2.1
    g3: Circle CenterX=10 CenterY=85.5 CenterZ=0 NormalX=0 NormalY=0 NormalZ=1 AngleXU=0 Radius=2.1
    g4: LineSegment [constr] StartX=10 StartY=0 StartZ=0 EndX=10 EndY=3 EndZ=0
  constraints (13):
    c: Distance(g0) = 32.5
    c: Vertical(g0)
    c: Distance(g1) = 50
    c: Coincident(g1,g0)
    c: Vertical(g1)
    c: Diameter(g2) = 4.2
    c: Coincident(g2,g0)
    c: Coincident(g3,g1)
    c: Equal(g3,g2)
    c: Symmetric(g-3,g-3,g4)
    c: Coincident(g4,g0)
    c: Vertical(g4)
    c: DistanceY(g4,g4) = 3
FEATURE [PartDesign::Hole] Hole004  label="P-PsMb-Drilled"
  BaseFeature = -> Pad009
  CustomThreadClearance = 0
  Depth = 25
  DepthType = 0
  Diameter = 4.2
  DrillForDepth = false
  DrillPoint = 1
  DrillPointAngle = 118
  HoleCutCountersinkAngle = 90
  HoleCutCustomValues = false
  HoleCutDepth = 0
  HoleCutDiameter = 8.4
  HoleCutType = 2
  ModelThread = false
  Profile = -> Sketch016
  Refine = true
  Suppressed = false
  Tapered = false
  TaperedAngle = 90
  ThreadClass = 0
  ThreadDepth = 25
  ThreadDepthType = 0
  ThreadDirection = 0
  ThreadFit = 0
  ThreadSize = 0
  ThreadType = 0
  Threaded = false
  UseCustomThreadClearance = false
FEATURE [Sketcher::SketchObject] Sketch017  label="Sk-PsMb-MountingScrew"
  ArcFitTolerance = 1e-06
  AttachmentSupport = -> [Hole004]
  ExternalGeometry = -> [Hole004]
  FullyConstrained = false
  MakeInternals = false
  MapMode = 5
  Placement = pos=(0,0,3) rot=(0,0,1;0rad)
  sketch-geometry (7):
    g0: LineSegment [constr] StartX=16.5538 StartY=9.97778 StartZ=0 EndX=3 EndY=9.97778 EndZ=0
    g1: LineSegment [constr] StartX=34.1077 StartY=9.97778 StartZ=0 EndX=20.5538 EndY=9.97778 EndZ=0
    g2: LineSegment [constr] StartX=20.5538 StartY=9.97778 StartZ=0 EndX=16.5538 EndY=9.97778 EndZ=0
    g3: ArcOfCircle CenterX=16.5538 CenterY=9.97778 CenterZ=0 NormalX=0 NormalY=0 NormalZ=1 AngleXU=0 Radius=2.07541 StartAngle=1.5708 EndAngle=4.71239
    g4: ArcOfCircle CenterX=20.5538 CenterY=9.97778 CenterZ=0 NormalX=0 NormalY=0 NormalZ=1 AngleXU=0 Radius=2.07541 StartAngle=4.71239 EndAngle=7.85398
    g5: LineSegment StartX=16.5538 StartY=12.0532 StartZ=0 EndX=20.5538 EndY=12.0532 EndZ=0
    g6: LineSegment StartX=16.5538 StartY=7.90237 StartZ=0 EndX=20.5538 EndY=7.90237 EndZ=0
  constraints (15):
    c: PointOnObject(g0,g-3)
    c: Coincident(g2,g0)
    c: Horizontal(g0)
    c: Coincident(g1,g2)
    c: Horizontal(g1)
    c: Horizontal(g2)
    c: Equal(g0,g1)
    c: Tangent(g3,g5) = 1.5708
    c: Tangent(g3,g6) = -1.5708
    c: Tangent(g4,g5) = 1.5708
    c: Tangent(g4,g6) = -1.5708
    c: Equal(g3,g4)
    c: DistanceX(g2,g2) = 4
    c: Coincident(g3,g0)
    c: Coincident(g1,g4)
FEATURE [PartDesign::Pocket] Pocket002  label="P-PsMb-Drilled2"
  BaseFeature = -> Hole004
  Direction = (0,0,-1)
  Length = 5
  Length2 = 5
  Profile = -> Sketch017
  ReferenceAxis = -> Sketch017 [N_Axis]
  Refine = true
  Suppressed = false
  Type = 1
FEATURE [PartDesign::Chamfer] Chamfer  label="P-PsMb-Drilled3"
  Angle = 45
  Base = -> Pocket002 [Edge6]
  BaseFeature = -> Pocket002
  ChamferType = 0
  FlipDirection = false
  Refine = true
  Size = 2
  Size2 = 1
  SupportTransform = false
  Suppressed = false
  UseAllEdges = false
FEATURE [PartDesign::Fillet] Fillet  label="P-PsMb"
  Base = -> Chamfer [Edge50,Edge25,Edge31,Edge54]
  BaseFeature = -> Chamfer
  Radius = 0.8
  Refine = true
  SupportTransform = false
  Suppressed = false
  UseAllEdges = false
FEATURE [Sketcher::SketchObject] Sketch018  label="Sk-PsMb-Front-Base"
  ArcFitTolerance = 1e-06
  AttachmentSupport = -> [XY_Plane004]
  FullyConstrained = true
  MakeInternals = false
  MapMode = 5
  sketch-geometry (5):
    g0: LineSegment StartX=3 StartY=0 StartZ=0 EndX=33.5 EndY=0 EndZ=0
    g1: LineSegment StartX=33.5 StartY=0 StartZ=0 EndX=33.5 EndY=20 EndZ=0
    g2: LineSegment StartX=33.5 StartY=20 StartZ=0 EndX=3 EndY=20 EndZ=0
    g3: LineSegment StartX=3 StartY=20 StartZ=0 EndX=3 EndY=0 EndZ=0
    g4: LineSegment [constr] StartX=0 StartY=0 StartZ=0 EndX=3 EndY=0 EndZ=0
  constraints (14):
    c: Horizontal(g0)
    c: Horizontal(g2)
    c: Vertical(g1)
    c: Vertical(g3)
    c: Distance(g1,g3) = 30.5
    c: Distance(g0,g2) = 20
    c: Coincident(g0,g3)
    c: Coincident(g0,g1)
    c: Coincident(g1,g2)
    c: Coincident(g3,g2)
    c: Coincident(g4,g-1)
    c: Coincident(g4,g0)
    c: Horizontal(g4)
    c: DistanceX(g4,g4) = 3
FEATURE [PartDesign::Pad] Pad010  label="P-PsMb-Front-Base"
  Direction = (0,0,1)
  Length = 2.8
  Length2 = 10
  Profile = -> Sketch018
  ReferenceAxis = -> Sketch018 [N_Axis]
  Refine = true
  Suppressed = false
  Type = 0
FEATURE [Sketcher::SketchObject] Sketch019  label="Sk-PsMb-Front-Low"
  ArcFitTolerance = 1e-06
  AttachmentSupport = -> [Pad010]
  ExternalGeometry = -> [Pad010]
  FullyConstrained = true
  MakeInternals = false
  MapMode = 5
  Placement = pos=(3,0,0) rot=(0.57735,-0.57735,-0.57735;2.0944rad)
  sketch-geometry (8):
    g0: LineSegment StartX=-20 StartY=0 StartZ=0 EndX=0 EndY=0 EndZ=0
    g1: LineSegment StartX=-4e-16 StartY=0 StartZ=0 EndX=-4e-16 EndY=12 EndZ=0
    g2: LineSegment StartX=-2 StartY=14 StartZ=0 EndX=-18 EndY=14 EndZ=0
    g3: LineSegment StartX=-20 StartY=12 StartZ=0 EndX=-20 EndY=0 EndZ=0
    g4: ArcOfCircle CenterX=-18 CenterY=12 CenterZ=0 NormalX=0 NormalY=0 NormalZ=1 AngleXU=0 Radius=2 StartAngle=1.5708 EndAngle=3.14159
    g5: GeomPoint [constr] X=-20 Y=14 Z=0
    g6: ArcOfCircle CenterX=-2 CenterY=12 CenterZ=0 NormalX=0 NormalY=0 NormalZ=1 AngleXU=0 Radius=2 StartAngle=0 EndAngle=1.5708
    g7: GeomPoint [constr] X=0 Y=14 Z=0
  constraints (18):
    c: Coincident(g0,g1)
    c: Coincident(g3,g0)
    c: Horizontal(g2)
    c: Vertical(g1)
    c: Vertical(g3)
    c: Coincident(g0,g-3)
    c: Coincident(g0,g-1)
    c: DistanceY(g3,g5) = 14
    c: PointOnObject(g5,g3)
    c: PointOnObject(g5,g2)
    c: Tangent(g3,g4) = -1.5708
    c: Tangent(g2,g4) = -1.5708
    c: PointOnObject(g7,g2)
    c: PointOnObject(g7,g1)
    c: Tangent(g2,g6) = -1.5708
    c: Tangent(g1,g6) = -1.5708
    c: Equal(g4,g6)
    c: Radius(g6) = 2
FEATURE [PartDesign::Pad] Pad011  label="P-PsMb-Front-Base-Low"
  BaseFeature = -> Pad010
  Direction = (-1,0,0)
  Length = 3
  Length2 = 10
  Profile = -> Sketch019
  ReferenceAxis = -> Sketch019 [N_Axis]
  Refine = true
  Suppressed = false
  Type = 0
FEATURE [Sketcher::SketchObject] Sketch020  label="Sk-PsMb-Front-High"
  ArcFitTolerance = 1e-06
  AttachmentSupport = -> [Pad011]
  ExternalGeometry = -> [Pad011]
  FullyConstrained = true
  MakeInternals = false
  MapMode = 5
  Placement = pos=(33.5,0,0) rot=(0.57735,0.57735,0.57735;2.0944rad)
  sketch-geometry (8):
    g0: LineSegment StartX=20 StartY=0 StartZ=0 EndX=20 EndY=92 EndZ=0
    g1: LineSegment StartX=18 StartY=94 StartZ=0 EndX=2 EndY=94 EndZ=0
    g2: LineSegment StartX=0 StartY=92 StartZ=0 EndX=0 EndY=0 EndZ=0
    g3: LineSegment StartX=0 StartY=0 StartZ=0 EndX=20 EndY=0 EndZ=0
    g4: ArcOfCircle CenterX=2 CenterY=92 CenterZ=0 NormalX=0 NormalY=0 NormalZ=1 AngleXU=0 Radius=2 StartAngle=1.5708 EndAngle=3.14159
    g5: GeomPoint [constr] X=0 Y=94 Z=0
    g6: ArcOfCircle CenterX=18 CenterY=92 CenterZ=0 NormalX=0 NormalY=0 NormalZ=1 AngleXU=0 Radius=2 StartAngle=3e-15 EndAngle=1.5708
    g7: GeomPoint [constr] X=20 Y=94 Z=0
  constraints (18):
    c: Coincident(g2,g3)
    c: Coincident(g3,g0)
    c: Vertical(g0)
    c: Vertical(g2)
    c: Horizontal(g1)
    c: Coincident(g0,g-3)
    c: Coincident(g-1,g2)
    c: PointOnObject(g5,g2)
    c: PointOnObject(g5,g1)
    c: Tangent(g2,g4) = -1.5708
    c: Tangent(g1,g4) = -1.5708
    c: PointOnObject(g7,g1)
    c: PointOnObject(g7,g0)
    c: Tangent(g1,g6) = -1.5708
    c: Tangent(g0,g6) = -1.5708
    c: Equal(g4,g6)
    c: Radius(g4) = 2
    c: DistanceY(g0,g1) = 94
FEATURE [PartDesign::Pad] Pad012  label="P-PsMb-Front-raw"
  BaseFeature = -> Pad011
  Direction = (1,0,0)
  Length = 3.5
  Length2 = 10
  Profile = -> Sketch020
  ReferenceAxis = -> Sketch020 [N_Axis]
  Refine = true
  Suppressed = false
  Type = 0
FEATURE [Sketcher::SketchObject] Sketch021  label="Sk-PsMb-Front-Ps-Screwholes"
  ArcFitTolerance = 1e-06
  AttachmentSupport = -> [Pad012]
  ExternalGeometry = -> [Pad012]
  FullyConstrained = true
  MakeInternals = false
  MapMode = 5
  Placement = pos=(37,0,0) rot=(0.57735,0.57735,0.57735;2.0944rad)
  sketch-geometry (5):
    g0: LineSegment [constr] StartX=10 StartY=4 StartZ=0 EndX=10 EndY=36.5 EndZ=0
    g1: LineSegment [constr] StartX=10 StartY=36.5 StartZ=0 EndX=10 EndY=86.5 EndZ=0
    g2: Circle CenterX=10 CenterY=36.5 CenterZ=0 NormalX=0 NormalY=0 NormalZ=1 AngleXU=0 Radius=2.1
    g3: Circle CenterX=10 CenterY=86.5 CenterZ=0 NormalX=0 NormalY=0 NormalZ=1 AngleXU=0 Radius=2.1
    g4: LineSegment [constr] StartX=10 StartY=0 StartZ=0 EndX=10 EndY=4 EndZ=0
  constraints (13):
    c: Distance(g0) = 32.5
    c: Vertical(g0)
    c: Distance(g1) = 50
    c: Coincident(g1,g0)
    c: Vertical(g1)
    c: Diameter(g2) = 4.2
    c: Coincident(g2,g0)
    c: Coincident(g3,g1)
    c: Equal(g3,g2)
    c: Symmetric(g-3,g-3,g4)
    c: Coincident(g4,g0)
    c: Vertical(g4)
    c: DistanceY(g4,g4) = 4
FEATURE [PartDesign::Hole] Hole005  label="P-PsMb-Front-Drilled"
  BaseFeature = -> Pad012
  CustomThreadClearance = 0
  Depth = 25
  DepthType = 0
  Diameter = 4.2
  DrillForDepth = false
  DrillPoint = 1
  DrillPointAngle = 118
  HoleCutCountersinkAngle = 90
  HoleCutCustomValues = false
  HoleCutDepth = 0
  HoleCutDiameter = 8.4
  HoleCutType = 2
  ModelThread = false
  Profile = -> Sketch021
  Refine = true
  Suppressed = false
  Tapered = false
  TaperedAngle = 90
  ThreadClass = 0
  ThreadDepth = 25
  ThreadDepthType = 0
  ThreadDirection = 0
  ThreadFit = 0
  ThreadSize = 0
  ThreadType = 0
  Threaded = false
  UseCustomThreadClearance = false
FEATURE [Sketcher::SketchObject] Sketch022  label="Sk-PsMb-Front-MountingScrew"
  ArcFitTolerance = 1e-06
  AttachmentSupport = -> [Hole005]
  ExternalGeometry = -> [Hole005]
  FullyConstrained = false
  MakeInternals = false
  MapMode = 5
  Placement = pos=(0,0,2.8) rot=(0,0,1;0rad)
  sketch-geometry (7):
    g0: LineSegment [constr] StartX=16.5538 StartY=9.97778 StartZ=0 EndX=3 EndY=9.97778 EndZ=0
    g1: LineSegment [constr] StartX=34.1077 StartY=9.97778 StartZ=0 EndX=20.5538 EndY=9.97778 EndZ=0
    g2: LineSegment [constr] StartX=20.5538 StartY=9.97778 StartZ=0 EndX=16.5538 EndY=9.97778 EndZ=0
    g3: ArcOfCircle CenterX=16.5538 CenterY=9.97778 CenterZ=0 NormalX=0 NormalY=0 NormalZ=1 AngleXU=0 Radius=2.07541 StartAngle=1.5708 EndAngle=4.71239
    g4: ArcOfCircle CenterX=20.5538 CenterY=9.97778 CenterZ=0 NormalX=0 NormalY=0 NormalZ=1 AngleXU=0 Radius=2.07541 StartAngle=4.71239 EndAngle=7.85398
    g5: LineSegment StartX=16.5538 StartY=12.0532 StartZ=0 EndX=20.5538 EndY=12.0532 EndZ=0
    g6: LineSegment StartX=16.5538 StartY=7.90237 StartZ=0 EndX=20.5538 EndY=7.90237 EndZ=0
  constraints (15):
    c: PointOnObject(g0,g-3)
    c: Coincident(g2,g0)
    c: Horizontal(g0)
    c: Coincident(g1,g2)
    c: Horizontal(g1)
    c: Horizontal(g2)
    c: Equal(g0,g1)
    c: Tangent(g3,g5) = 1.5708
    c: Tangent(g3,g6) = -1.5708
    c: Tangent(g4,g5) = 1.5708
    c: Tangent(g4,g6) = -1.5708
    c: Equal(g3,g4)
    c: DistanceX(g2,g2) = 4
    c: Coincident(g3,g0)
    c: Coincident(g1,g4)
FEATURE [PartDesign::Pocket] Pocket003  label="P-PsMb-Front-Drilled2"
  BaseFeature = -> Hole005
  Direction = (0,0,-1)
  Length = 5
  Length2 = 5
  Profile = -> Sketch022
  ReferenceAxis = -> Sketch022 [N_Axis]
  Refine = true
  Suppressed = false
  Type = 1
FEATURE [PartDesign::Chamfer] Chamfer001  label="P-PsMb-Front-Drilled3"
  Angle = 45
  Base = -> Pocket003 [Edge6]
  BaseFeature = -> Pocket003
  ChamferType = 0
  FlipDirection = false
  Refine = true
  Size = 2
  Size2 = 1
  SupportTransform = false
  Suppressed = false
  UseAllEdges = false
FEATURE [PartDesign::Fillet] Fillet001  label="P-PsMb-Front"
  Base = -> Chamfer001 [Edge50,Edge25,Edge31,Edge54]
  BaseFeature = -> Chamfer001
  Radius = 0.8
  Refine = true
  SupportTransform = false
  Suppressed = false
  UseAllEdges = false
FEATURE [PartDesign::Body] Body004  label="B-Power Supply Mounting Brace - High - ShallowBase"
  AllowCompound = false
  Group = -> [Sketch018,Pad010,Sketch019,Pad011,Sketch020,Pad012,Sketch021,Hole005,Sketch022,Pocket003,Chamfer001,Fillet001]
  Origin = -> Origin004
  Placement = pos=(0,-21.9,0) rot=(0,0,1;0rad)
  Tip = -> Fillet001
FEATURE [Sketcher::SketchObject] Sketch023  label="Sk-Bracket-High-Shield"
  ArcFitTolerance = 1e-06
  AttachmentSupport = -> [XY_Plane005]
  FullyConstrained = true
  MakeInternals = false
  MapMode = 5
  sketch-geometry (17):
    g0: LineSegment StartX=32 StartY=34.5 StartZ=0 EndX=12 EndY=34.5 EndZ=0
    g1: LineSegment StartX=6.7528e-12 StartY=22.5 StartZ=0 EndX=6.7528e-12 EndY=3 EndZ=0
    g2: LineSegment StartX=2 StartY=5 StartZ=0 EndX=2 EndY=22.5 EndZ=0
    g3: LineSegment StartX=12 StartY=32.5 StartZ=0 EndX=32 EndY=32.5 EndZ=0
    g4: LineSegment StartX=32 StartY=32.5 StartZ=0 EndX=32 EndY=34.5 EndZ=0
    g5: ArcOfCircle CenterX=12 CenterY=22.5 CenterZ=0 NormalX=0 NormalY=0 NormalZ=1 AngleXU=0 Radius=12 StartAngle=1.5708 EndAngle=3.14159
    g6: GeomPoint [constr] X=0 Y=34.5 Z=0
    g7: ArcOfCircle CenterX=12 CenterY=22.5 CenterZ=0 NormalX=0 NormalY=0 NormalZ=1 AngleXU=0 Radius=10 StartAngle=1.5708 EndAngle=3.14159
    g8: GeomPoint [constr] X=2 Y=32.5 Z=0
    g9: LineSegment StartX=3 StartY=6.0982e-12 StartZ=0 EndX=32 EndY=6.0982e-12 EndZ=0
    g10: LineSegment StartX=32 StartY=6.0982e-12 StartZ=0 EndX=32 EndY=2 EndZ=0
    g11: LineSegment StartX=32 StartY=2 StartZ=0 EndX=5 EndY=2 EndZ=0
    g12: LineSegment [constr] StartX=32 StartY=32.5 StartZ=0 EndX=32 EndY=2 EndZ=0
    g13: ArcOfCircle CenterX=5 CenterY=5 CenterZ=0 NormalX=0 NormalY=0 NormalZ=1 AngleXU=0 Radius=3 StartAngle=3.14159 EndAngle=4.71239
    g14: GeomPoint [constr] X=2 Y=2 Z=0
    g15: ArcOfCircle CenterX=3 CenterY=3 CenterZ=0 NormalX=0 NormalY=0 NormalZ=1 AngleXU=0 Radius=3 StartAngle=3.14159 EndAngle=4.71239
    g16: GeomPoint [constr] X=0 Y=0 Z=0
  constraints (41):
    c: Horizontal(g0)
    c: Horizontal(g3)
    c: Coincident(g3,g4)
    c: Coincident(g4,g0)
    c: Vertical(g4)
    c: Vertical(g1)
    c: Vertical(g2)
    c: PointOnObject(g6,g0)
    c: PointOnObject(g6,g1)
    c: Tangent(g0,g5) = -1.5708
    c: Tangent(g1,g5) = -1.5708
    c: PointOnObject(g8,g3)
    c: PointOnObject(g8,g2)
    c: Tangent(g3,g7) = 1.5708
    c: Tangent(g2,g7) = 1.5708
    c: DistanceX(g16,g14) = 2
    c: Coincident(g5,g7)
    c: Radius(g7) = 10
    c: DistanceY(g16,g1) = 22.5
    c: Coincident(g9,g10)
    c: Coincident(g10,g11)
    c: Vertical(g10)
    c: Horizontal(g9)
    c: Horizontal(g11)
    c: Equal(g4,g10)
    c: DistanceY(g10,g3) = 30.5
    c: DistanceX(g0,g0) = 20
    c: Coincident(g12,g3)
    c: Coincident(g12,g10)
    c: Vertical(g12)
    c: Coincident(g16,g-1)
    c: PointOnObject(g14,g2)
    c: PointOnObject(g14,g11)
    c: Tangent(g2,g13) = 1.5708
    c: Tangent(g11,g13) = 1.5708
    c: PointOnObject(g16,g1)
    c: PointOnObject(g16,g9)
    c: Tangent(g1,g15) = -1.5708
    c: Tangent(g9,g15) = -1.5708
    c: Equal(g13,g15)
    c: Radius(g13) = 3
FEATURE [PartDesign::Pad] Pad013  label="P-Bracket-High-Shield"
  Direction = (0,0,1)
  Length = 115.5
  Length2 = 10
  Profile = -> Sketch023
  ReferenceAxis = -> Sketch023 [N_Axis]
  Refine = true
  Suppressed = false
  Type = 0
FEATURE [Sketcher::SketchObject] Sketch026  label="Sk-Bracket-High-LED-Window"
  ArcFitTolerance = 1e-06
  AttachmentSupport = -> [Pad013]
  ExternalGeometry = -> [Pad013]
  FullyConstrained = true
  MakeInternals = false
  MapMode = 5
  Placement = pos=(0,34.5,0) rot=(0,0.707107,0.707107;3.14159rad)
  sketch-geometry (6):
    g0: LineSegment StartX=-32 StartY=0 StartZ=0 EndX=-12 EndY=0 EndZ=0
    g1: LineSegment StartX=-12 StartY=0 StartZ=0 EndX=-12 EndY=7 EndZ=0
    g2: LineSegment StartX=-15 StartY=10 StartZ=0 EndX=-32 EndY=10 EndZ=0
    g3: LineSegment StartX=-32 StartY=10 StartZ=0 EndX=-32 EndY=0 EndZ=0
    g4: ArcOfCircle CenterX=-15 CenterY=7 CenterZ=0 NormalX=0 NormalY=0 NormalZ=1 AngleXU=0 Radius=3 StartAngle=3.33997e-11 EndAngle=1.5708
    g5: GeomPoint [constr] X=-12 Y=10 Z=0
  constraints (14):
    c: Coincident(g0,g1)
    c: Coincident(g2,g3)
    c: Coincident(g3,g0)
    c: Horizontal(g2)
    c: Vertical(g1)
    c: Vertical(g3)
    c: Coincident(g0,g-3)
    c: Coincident(g-3,g0)
    c: DistanceY(g3,g3) = 10
    c: PointOnObject(g5,g2)
    c: PointOnObject(g5,g1)
    c: Tangent(g2,g4) = -1.5708
    c: Tangent(g1,g4) = -1.5708
    c: Radius(g4) = 3
FEATURE [PartDesign::Pocket] Pocket004  label="P-Bracket-High-LED"
  BaseFeature = -> Pad013
  Direction = (0,-1,2e-16)
  Length = 5
  Length2 = 5
  Profile = -> Sketch026
  ReferenceAxis = -> Sketch026 [N_Axis]
  Refine = true
  Suppressed = false
  Type = 2
FEATURE [Sketcher::SketchObject] Sketch027  label="Sk-Bracket-High-CableWindow"
  ArcFitTolerance = 1e-06
  AttachmentSupport = -> [Pocket004]
  ExternalGeometry = -> [Pocket004]
  FullyConstrained = true
  MakeInternals = false
  MapMode = 5
  Placement = pos=(0,6.0982e-12,0) rot=(1,0,0;1.5708rad)
  sketch-geometry (16):
    g0: LineSegment StartX=2 StartY=115.5 StartZ=0 EndX=2 EndY=106.5 EndZ=0
    g1: LineSegment StartX=5 StartY=103.5 StartZ=0 EndX=9 EndY=103.5 EndZ=0
    g2: LineSegment StartX=12 StartY=106.5 StartZ=0 EndX=12 EndY=115.5 EndZ=0
    g3: LineSegment StartX=12 StartY=115.5 StartZ=0 EndX=2 EndY=115.5 EndZ=0
    g4: ArcOfCircle CenterX=5 CenterY=106.5 CenterZ=0 NormalX=0 NormalY=0 NormalZ=1 AngleXU=0 Radius=3 StartAngle=3.14159 EndAngle=4.71239
    g5: GeomPoint [constr] X=2 Y=103.5 Z=0
    g6: ArcOfCircle CenterX=9 CenterY=106.5 CenterZ=0 NormalX=0 NormalY=0 NormalZ=1 AngleXU=0 Radius=3 StartAngle=4.71239 EndAngle=6.28319
    g7: GeomPoint [constr] X=12 Y=103.5 Z=0
    g8: LineSegment [constr] StartX=2 StartY=1.8e-15 StartZ=0 EndX=12 EndY=1.8e-15 EndZ=0
    g9: LineSegment [constr] StartX=12 StartY=1.8e-15 StartZ=0 EndX=12 EndY=9 EndZ=0
    g10: LineSegment [constr] StartX=9 StartY=12 StartZ=0 EndX=5 EndY=12 EndZ=0
    g11: LineSegment [constr] StartX=2 StartY=9 StartZ=0 EndX=2 EndY=1.8e-15 EndZ=0
    g12: ArcOfCircle [constr] CenterX=5 CenterY=9 CenterZ=0 NormalX=0 NormalY=0 NormalZ=1 AngleXU=0 Radius=3 StartAngle=1.5708 EndAngle=3.14159
    g13: GeomPoint [constr] X=2 Y=12 Z=0
    g14: ArcOfCircle [constr] CenterX=9 CenterY=9 CenterZ=0 NormalX=0 NormalY=0 NormalZ=1 AngleXU=0 Radius=3 StartAngle=1e-16 EndAngle=1.5708
    g15: GeomPoint [constr] X=12 Y=12 Z=0
  constraints (38):
    c: Coincident(g2,g3)
    c: Coincident(g3,g0)
    c: Vertical(g0)
    c: Vertical(g2)
    c: Horizontal(g1)
    c: Horizontal(g3)
    c: Distance(g0,g2) = 10
    c: Distance(g5,g3) = 12
    c: Coincident(g0,g-5)
    c: PointOnObject(g5,g0)
    c: PointOnObject(g5,g1)
    c: Tangent(g0,g4) = -1.5708
    c: Tangent(g1,g4) = -1.5708
    c: PointOnObject(g7,g2)
    c: PointOnObject(g7,g1)
    c: Tangent(g2,g6) = -1.5708
    c: Tangent(g1,g6) = -1.5708
    c: Equal(g4,g6)
    c: Radius(g4) = 3
    c: Coincident(g8,g9)
    c: Coincident(g11,g8)
    c: Horizontal(g8)
    c: Horizontal(g10)
    c: Vertical(g9)
    c: Vertical(g11)
    c: Coincident(g8,g-5)
    c: PointOnObject(g13,g11)
    c: PointOnObject(g13,g10)
    c: Tangent(g11,g12) = -1.5708
    c: Tangent(g10,g12) = -1.5708
    c: PointOnObject(g15,g10)
    c: PointOnObject(g15,g9)
    c: Tangent(g10,g14) = -1.5708
    c: Tangent(g9,g14) = -1.5708
    c: Equal(g6,g14)
    c: Equal(g14,g12)
    c: Equal(g1,g10)
    c: Equal(g2,g9)
FEATURE [PartDesign::Pocket] Pocket005  label="P-Bracket-High-Windows"
  BaseFeature = -> Pocket004
  Direction = (0,1,-2e-16)
  Length = 5
  Length2 = 5
  Profile = -> Sketch027
  ReferenceAxis = -> Sketch027 [N_Axis]
  Refine = true
  Suppressed = false
  Type = 1
FEATURE [Sketcher::SketchObject] Sketch028  label="B-Power Supply Bracket - High - Screwplate"
  ArcFitTolerance = 1e-06
  AttachmentSupport = -> [Pocket005]
  ExternalGeometry = -> [Pocket005]
  FullyConstrained = false
  MakeInternals = false
  MapMode = 5
  Placement = pos=(0,0,0) rot=(1,0,0;3.14159rad)
  sketch-geometry (28):
    g0: ArcOfCircle CenterX=12 CenterY=-22.5 CenterZ=0 NormalX=0 NormalY=0 NormalZ=1 AngleXU=0 Radius=12 StartAngle=3.14159 EndAngle=4.71239
    g1: ArcOfCircle CenterX=3 CenterY=-3 CenterZ=0 NormalX=0 NormalY=0 NormalZ=1 AngleXU=0 Radius=3 StartAngle=1.5708 EndAngle=3.14159
    g2: LineSegment StartX=3 StartY=-6.1413e-12 StartZ=0 EndX=32 EndY=-6.0982e-12 EndZ=0
    g3: LineSegment StartX=6.7528e-12 StartY=-3 StartZ=0 EndX=6.7528e-12 EndY=-22.5 EndZ=0
    g4: LineSegment StartX=12 StartY=-34.5 StartZ=0 EndX=32 EndY=-34.5 EndZ=0
    g5: LineSegment [constr] StartX=12 StartY=-34.5 StartZ=0 EndX=12 EndY=-14.5 EndZ=0
    g6: LineSegment [constr] StartX=12 StartY=-14.5 StartZ=0 EndX=12 EndY=-6.1284e-12 EndZ=0
    g7: LineSegment [constr] StartX=12 StartY=-14.5 StartZ=0 EndX=44.5 EndY=-14.5 EndZ=0
    g8: Circle CenterX=44.5 CenterY=-14.5 CenterZ=0 NormalX=0 NormalY=0 NormalZ=1 AngleXU=0 Radius=2.1
    g9: ArcOfCircle CenterX=44.5 CenterY=-14.5 CenterZ=0 NormalX=0 NormalY=0 NormalZ=1 AngleXU=0 Radius=7.1 StartAngle=5.44132 EndAngle=7.36124
    g10: LineSegment StartX=32.9461 StartY=-0.237919 StartZ=0 EndX=47.8586 EndY=-8.24461 EndZ=0
    g11: ArcOfCircle CenterX=32 CenterY=-2 CenterZ=0 NormalX=0 NormalY=0 NormalZ=1 AngleXU=0 Radius=2 StartAngle=1.07806 EndAngle=1.5708
    g12: LineSegment StartX=33.3321 StartY=-33.9918 StartZ=0 EndX=49.2291 EndY=-19.7958 EndZ=0
    g13: ArcOfCircle CenterX=32 CenterY=-32.5 CenterZ=0 NormalX=0 NormalY=0 NormalZ=1 AngleXU=0 Radius=2 StartAngle=4.71239 EndAngle=5.44132
    g14: LineSegment [constr] StartX=44.5 StartY=-14.5 StartZ=0 EndX=46.6 EndY=-14.5 EndZ=0
    g15: LineSegment [constr] StartX=46.6 StartY=-14.5 StartZ=0 EndX=51.6 EndY=-14.5 EndZ=0
    g16: LineSegment [constr] StartX=32 StartY=-32.5 StartZ=0 EndX=32 EndY=-28.0326 EndZ=0
    g17: LineSegment [constr] StartX=32 StartY=-2 StartZ=0 EndX=32 EndY=-5.34387 EndZ=0
    g18: LineSegment StartX=32 StartY=-5.34387 StartZ=0 EndX=32 EndY=-28.0326 EndZ=0
    g19: ArcOfCircle CenterX=44.5 CenterY=-14.5 CenterZ=0 NormalX=0 NormalY=0 NormalZ=1 AngleXU=0 Radius=7.1 StartAngle=2.30124 EndAngle=4.21814
    g20: ArcOfCircle CenterX=38.4285 CenterY=-7.72158 CenterZ=0 NormalX=0 NormalY=0 NormalZ=1 AngleXU=0 Radius=2 StartAngle=5.44283 EndAngle=7.36124
    g21: ArcOfCircle CenterX=40.1833 CenterY=-22.511 CenterZ=0 NormalX=0 NormalY=0 NormalZ=1 AngleXU=0 Radius=2 StartAngle=5.44132 EndAngle=7.35974
    g22: ArcOfCircle CenterX=34 CenterY=-28.0326 CenterZ=0 NormalX=0 NormalY=0 NormalZ=1 AngleXU=0 Radius=2 StartAngle=3.14159 EndAngle=5.44132
    g23: ArcOfCircle CenterX=34 CenterY=-5.34387 CenterZ=0 NormalX=0 NormalY=0 NormalZ=1 AngleXU=0 Radius=2 StartAngle=1.07806 EndAngle=3.14159
    g24: LineSegment StartX=34.9461 StartY=-3.58178 StartZ=0 EndX=39.3746 EndY=-5.9595 EndZ=0
    g25: LineSegment StartX=35.3321 StartY=-29.5244 StartZ=0 EndX=41.5154 EndY=-24.0027 EndZ=0
    g26: LineSegment [constr] StartX=32 StartY=-2 StartZ=0 EndX=34.9461 EndY=-3.58178 EndZ=0
    g27: LineSegment [constr] StartX=32 StartY=-32.5 StartZ=0 EndX=35.3321 EndY=-29.5244 EndZ=0
  constraints (67):
    c: Coincident(g0,g-4)
    c: Coincident(g0,g-4)
    c: Coincident(g1,g-3)
    c: Coincident(g1,g-3)
    c: Coincident(g2,g1)
    c: Coincident(g2,g-5)
    c: Coincident(g3,g1)
    c: Coincident(g3,g0)
    c: Vertical(g3)
    c: Coincident(g4,g0)
    c: Coincident(g4,g-6)
    c: Coincident(g5,g0)
    c: PointOnObject(g6,g2)
    c: Coincident(g5,g6)
    c: Vertical(g5)
    c: Vertical(g6)
    c: DistanceY(g5,g-5) = 12.5
    c: Distance(g7) = 32.5
    c: Coincident(g7,g5)
    c: Horizontal(g7)
    c: Diameter(g8) = 4.2
    c: Coincident(g8,g7)
    c: Coincident(g9,g7)
    c: Tangent(g11,g2) = 1.5708
    c: Tangent(g11,g10) = 1.5708
    c: Tangent(g10,g9) = 1.5708
    c: Tangent(g13,g4) = -1.5708
    c: Tangent(g13,g12) = -1.5708
    c: Tangent(g12,g9) = -1.5708
    c: Coincident(g14,g7)
    c: PointOnObject(g15,g9)
    c: Coincident(g14,g15)
    c: Horizontal(g14)
    c: Horizontal(g15)
    c: PointOnObject(g14,g8)
    c: DistanceX(g15,g15) = 5
    c: Coincident(g16,g13)
    c: Vertical(g16)
    c: Coincident(g17,g-5)
    c: Vertical(g17)
    c: Coincident(g18,g17)
    c: Coincident(g18,g16)
    c: Coincident(g19,g7)
    c: Equal(g19,g9)
    c: Coincident(g22,g16)
    c: Coincident(g23,g17)
    c: Tangent(g25,g21) = -1.5708
    c: Tangent(g20,g19) = 1.5708
    c: Tangent(g24,g20) = 1.5708
    c: Tangent(g24,g23) = 1.5708
    c: Tangent(g23,g18)
    c: Tangent(g22,g18)
    c: Tangent(g25,g22) = -1.5708
    c: Parallel(g25,g12)
    c: Parallel(g24,g10)
    c: Coincident(g26,g17)
    c: Coincident(g26,g23)
    c: Coincident(g27,g13)
    c: Tangent(g27,g22) = -1.5708
    c: Tangent(g21,g19) = 1.5708
    c: Parallel(g26,g10)
    c: Equal(g13,g11)
    c: Radius(g23) = 2
    c: Equal(g23,g20)
    c: Equal(g20,g21)
    c: Equal(g21,g22)
    c: Coincident(g13,g-6)
FEATURE [PartDesign::Pad] Pad014  label="P-Power Supply Bracket - High - raw"
  BaseFeature = -> Pocket005
  Direction = (0,0,-1)
  Length = 2.5
  Length2 = 10
  Profile = -> Sketch028
  ReferenceAxis = -> Sketch028 [N_Axis]
  Refine = true
  Suppressed = false
  Type = 0
FEATURE [Sketcher::SketchObject] Sketch029  label="Sk-Bracket-High-Shield001"
  ArcFitTolerance = 1e-06
  AttachmentSupport = -> [XY_Plane006]
  FullyConstrained = true
  MakeInternals = false
  MapMode = 5
  sketch-geometry (17):
    g0: LineSegment StartX=32 StartY=34.5 StartZ=0 EndX=12 EndY=34.5 EndZ=0
    g1: LineSegment StartX=6.7528e-12 StartY=22.5 StartZ=0 EndX=6.7528e-12 EndY=3 EndZ=0
    g2: LineSegment StartX=2 StartY=5 StartZ=0 EndX=2 EndY=22.5 EndZ=0
    g3: LineSegment StartX=12 StartY=32.5 StartZ=0 EndX=32 EndY=32.5 EndZ=0
    g4: LineSegment StartX=32 StartY=32.5 StartZ=0 EndX=32 EndY=34.5 EndZ=0
    g5: ArcOfCircle CenterX=12 CenterY=22.5 CenterZ=0 NormalX=0 NormalY=0 NormalZ=1 AngleXU=0 Radius=12 StartAngle=1.5708 EndAngle=3.14159
    g6: GeomPoint [constr] X=0 Y=34.5 Z=0
    g7: ArcOfCircle CenterX=12 CenterY=22.5 CenterZ=0 NormalX=0 NormalY=0 NormalZ=1 AngleXU=0 Radius=10 StartAngle=1.5708 EndAngle=3.14159
    g8: GeomPoint [constr] X=2 Y=32.5 Z=0
    g9: LineSegment StartX=3 StartY=6.0982e-12 StartZ=0 EndX=32 EndY=6.0982e-12 EndZ=0
    g10: LineSegment StartX=32 StartY=6.0982e-12 StartZ=0 EndX=32 EndY=2 EndZ=0
    g11: LineSegment StartX=32 StartY=2 StartZ=0 EndX=5 EndY=2 EndZ=0
    g12: LineSegment [constr] StartX=32 StartY=32.5 StartZ=0 EndX=32 EndY=2 EndZ=0
    g13: ArcOfCircle CenterX=5 CenterY=5 CenterZ=0 NormalX=0 NormalY=0 NormalZ=1 AngleXU=0 Radius=3 StartAngle=3.14159 EndAngle=4.71239
    g14: GeomPoint [constr] X=2 Y=2 Z=0
    g15: ArcOfCircle CenterX=3 CenterY=3 CenterZ=0 NormalX=0 NormalY=0 NormalZ=1 AngleXU=0 Radius=3 StartAngle=3.14159 EndAngle=4.71239
    g16: GeomPoint [constr] X=0 Y=0 Z=0
  constraints (41):
    c: Horizontal(g0)
    c: Horizontal(g3)
    c: Coincident(g3,g4)
    c: Coincident(g4,g0)
    c: Vertical(g4)
    c: Vertical(g1)
    c: Vertical(g2)
    c: PointOnObject(g6,g0)
    c: PointOnObject(g6,g1)
    c: Tangent(g0,g5) = -1.5708
    c: Tangent(g1,g5) = -1.5708
    c: PointOnObject(g8,g3)
    c: PointOnObject(g8,g2)
    c: Tangent(g3,g7) = 1.5708
    c: Tangent(g2,g7) = 1.5708
    c: DistanceX(g16,g14) = 2
    c: Coincident(g5,g7)
    c: Radius(g7) = 10
    c: DistanceY(g16,g1) = 22.5
    c: Coincident(g9,g10)
    c: Coincident(g10,g11)
    c: Vertical(g10)
    c: Horizontal(g9)
    c: Horizontal(g11)
    c: Equal(g4,g10)
    c: DistanceY(g10,g3) = 30.5
    c: DistanceX(g0,g0) = 20
    c: Coincident(g12,g3)
    c: Coincident(g12,g10)
    c: Vertical(g12)
    c: Coincident(g16,g-1)
    c: PointOnObject(g14,g2)
    c: PointOnObject(g14,g11)
    c: Tangent(g2,g13) = 1.5708
    c: Tangent(g11,g13) = 1.5708
    c: PointOnObject(g16,g1)
    c: PointOnObject(g16,g9)
    c: Tangent(g1,g15) = -1.5708
    c: Tangent(g9,g15) = -1.5708
    c: Equal(g13,g15)
    c: Radius(g13) = 3
FEATURE [PartDesign::Pad] Pad015  label="P-Bracket-High-Shield001"
  Direction = (0,0,1)
  Length = 115.5
  Length2 = 10
  Profile = -> Sketch029
  ReferenceAxis = -> Sketch029 [N_Axis]
  Refine = true
  Suppressed = false
  Type = 0
FEATURE [Sketcher::SketchObject] Sketch030  label="Sk-Bracket-High-LED-Window001"
  ArcFitTolerance = 1e-06
  AttachmentSupport = -> [Pad015]
  ExternalGeometry = -> [Pad015]
  FullyConstrained = true
  MakeInternals = false
  MapMode = 5
  Placement = pos=(0,34.5,0) rot=(0,0.707107,0.707107;3.14159rad)
  sketch-geometry (6):
    g0: LineSegment StartX=-32 StartY=0 StartZ=0 EndX=-12 EndY=0 EndZ=0
    g1: LineSegment StartX=-12 StartY=0 StartZ=0 EndX=-12 EndY=7 EndZ=0
    g2: LineSegment StartX=-15 StartY=10 StartZ=0 EndX=-32 EndY=10 EndZ=0
    g3: LineSegment StartX=-32 StartY=10 StartZ=0 EndX=-32 EndY=0 EndZ=0
    g4: ArcOfCircle CenterX=-15 CenterY=7 CenterZ=0 NormalX=0 NormalY=0 NormalZ=1 AngleXU=0 Radius=3 StartAngle=3.33997e-11 EndAngle=1.5708
    g5: GeomPoint [constr] X=-12 Y=10 Z=0
  constraints (14):
    c: Coincident(g0,g1)
    c: Coincident(g2,g3)
    c: Coincident(g3,g0)
    c: Horizontal(g2)
    c: Vertical(g1)
    c: Vertical(g3)
    c: Coincident(g0,g-3)
    c: Coincident(g-3,g0)
    c: DistanceY(g3,g3) = 10
    c: PointOnObject(g5,g2)
    c: PointOnObject(g5,g1)
    c: Tangent(g2,g4) = -1.5708
    c: Tangent(g1,g4) = -1.5708
    c: Radius(g4) = 3
FEATURE [PartDesign::Pocket] Pocket006  label="P-Bracket-High-LED001"
  BaseFeature = -> Pad015
  Direction = (0,-1,2e-16)
  Length = 5
  Length2 = 5
  Profile = -> Sketch030
  ReferenceAxis = -> Sketch030 [N_Axis]
  Refine = true
  Suppressed = false
  Type = 2
FEATURE [Sketcher::SketchObject] Sketch031  label="Sk-Bracket-High-CableWindow001"
  ArcFitTolerance = 1e-06
  AttachmentSupport = -> [Pocket006]
  ExternalGeometry = -> [Pocket006]
  FullyConstrained = true
  MakeInternals = false
  MapMode = 5
  Placement = pos=(0,6.0982e-12,0) rot=(1,0,0;1.5708rad)
  sketch-geometry (14):
    g0: LineSegment [constr] StartX=2 StartY=115.5 StartZ=0 EndX=2 EndY=106.5 EndZ=0
    g1: LineSegment [constr] StartX=5 StartY=103.5 StartZ=0 EndX=9 EndY=103.5 EndZ=0
    g2: LineSegment [constr] StartX=12 StartY=106.5 StartZ=0 EndX=12 EndY=115.5 EndZ=0
    g3: LineSegment [constr] StartX=12 StartY=115.5 StartZ=0 EndX=2 EndY=115.5 EndZ=0
    g4: ArcOfCircle [constr] CenterX=5 CenterY=106.5 CenterZ=0 NormalX=0 NormalY=0 NormalZ=1 AngleXU=0 Radius=3 StartAngle=3.14159 EndAngle=4.71239
    g5: GeomPoint [constr] X=2 Y=103.5 Z=0
    g6: ArcOfCircle [constr] CenterX=9 CenterY=106.5 CenterZ=0 NormalX=0 NormalY=0 NormalZ=1 AngleXU=0 Radius=3 StartAngle=4.71239 EndAngle=6.28319
    g7: GeomPoint [constr] X=12 Y=103.5 Z=0
    g8: LineSegment StartX=2 StartY=1.8e-15 StartZ=0 EndX=32 EndY=0 EndZ=0
    g9: LineSegment StartX=32 StartY=0 StartZ=0 EndX=32 EndY=12 EndZ=0
    g10: LineSegment StartX=32 StartY=12 StartZ=0 EndX=5 EndY=12 EndZ=0
    g11: LineSegment StartX=2 StartY=9 StartZ=0 EndX=2 EndY=1.8e-15 EndZ=0
    g12: ArcOfCircle CenterX=5 CenterY=9 CenterZ=0 NormalX=0 NormalY=0 NormalZ=1 AngleXU=0 Radius=3 StartAngle=1.5708 EndAngle=3.14159
    g13: GeomPoint [constr] X=2 Y=12 Z=0
  constraints (33):
    c: Coincident(g2,g3)
    c: Coincident(g3,g0)
    c: Vertical(g0)
    c: Vertical(g2)
    c: Horizontal(g1)
    c: Horizontal(g3)
    c: Distance(g0,g2) = 10
    c: Distance(g5,g3) = 12
    c: Coincident(g0,g-5)
    c: PointOnObject(g5,g0)
    c: PointOnObject(g5,g1)
    c: Tangent(g0,g4) = -1.5708
    c: Tangent(g1,g4) = -1.5708
    c: PointOnObject(g7,g2)
    c: PointOnObject(g7,g1)
    c: Tangent(g2,g6) = -1.5708
    c: Tangent(g1,g6) = -1.5708
    c: Equal(g4,g6)
    c: Radius(g4) = 3
    c: Coincident(g8,g9)
    c: Coincident(g11,g8)
    c: Horizontal(g10)
    c: Vertical(g9)
    c: Vertical(g11)
    c: Coincident(g8,g-5)
    c: PointOnObject(g13,g11)
    c: PointOnObject(g13,g10)
    c: Tangent(g11,g12) = -1.5708
    c: Tangent(g10,g12) = -1.5708
    c: Coincident(g10,g9)
    c: Coincident(g8,g-4)
    c: Equal(g12,g4)
    c: Equal(g0,g11)
FEATURE [PartDesign::Pocket] Pocket007  label="P-Bracket-High-Windows001"
  BaseFeature = -> Pocket006
  Direction = (0,1,-2e-16)
  Length = 5
  Length2 = 5
  Profile = -> Sketch031
  ReferenceAxis = -> Sketch031 [N_Axis]
  Refine = true
  Suppressed = false
  Type = 1
FEATURE [Sketcher::SketchObject] Sketch032  label="B-Power Supply Bracket - High - Screwplate001"
  ArcFitTolerance = 1e-06
  AttachmentSupport = -> [Pocket007]
  ExternalGeometry = -> [Pocket007]
  FullyConstrained = true
  MakeInternals = false
  MapMode = 5
  Placement = pos=(0,0,115.5) rot=(0,0,1;0rad)
  sketch-geometry (30):
    g0: ArcOfCircle CenterX=12 CenterY=22.5 CenterZ=0 NormalX=0 NormalY=0 NormalZ=1 AngleXU=0 Radius=12 StartAngle=1.5708 EndAngle=3.14159
    g1: ArcOfCircle CenterX=3 CenterY=3 CenterZ=0 NormalX=0 NormalY=0 NormalZ=1 AngleXU=0 Radius=3 StartAngle=3.14159 EndAngle=4.71239
    g2: LineSegment StartX=3 StartY=6.0982e-12 StartZ=0 EndX=32 EndY=6.0982e-12 EndZ=0
    g3: LineSegment StartX=6.7528e-12 StartY=3 StartZ=0 EndX=0 EndY=22.5 EndZ=0
    g4: LineSegment StartX=12 StartY=34.5 StartZ=0 EndX=32 EndY=34.5 EndZ=0
    g5: LineSegment [constr] StartX=12 StartY=34.5 StartZ=0 EndX=12 EndY=14.5 EndZ=0
    g6: LineSegment [constr] StartX=12 StartY=14.5 StartZ=0 EndX=44.5 EndY=14.5 EndZ=0
    g7: Circle CenterX=44.5 CenterY=14.5 CenterZ=0 NormalX=0 NormalY=0 NormalZ=1 AngleXU=0 Radius=2.1
    g8: ArcOfCircle CenterX=44.5 CenterY=14.5 CenterZ=0 NormalX=0 NormalY=0 NormalZ=1 AngleXU=0 Radius=7.1 StartAngle=5.20513 EndAngle=7.12505
    g9: LineSegment StartX=32.9461 StartY=0.237919 StartZ=0 EndX=47.8586 EndY=8.24461 EndZ=0
    g10: ArcOfCircle CenterX=32 CenterY=2 CenterZ=0 NormalX=0 NormalY=0 NormalZ=1 AngleXU=0 Radius=2 StartAngle=4.71239 EndAngle=5.20513
    g11: LineSegment StartX=33.3321 StartY=33.9918 StartZ=0 EndX=49.2291 EndY=19.7958 EndZ=0
    g12: ArcOfCircle CenterX=32 CenterY=32.5 CenterZ=0 NormalX=0 NormalY=0 NormalZ=1 AngleXU=0 Radius=2 StartAngle=0.841863 EndAngle=1.5708
    g13: LineSegment [constr] StartX=44.5 StartY=14.5 StartZ=0 EndX=46.6 EndY=14.5 EndZ=0
    g14: LineSegment [constr] StartX=46.6 StartY=14.5 StartZ=0 EndX=51.6 EndY=14.5 EndZ=0
    g15: LineSegment [constr] StartX=32 StartY=32.5 StartZ=0 EndX=32 EndY=28.0326 EndZ=0
    g16: LineSegment [constr] StartX=32 StartY=2 StartZ=0 EndX=32 EndY=5.34387 EndZ=0
    g17: LineSegment StartX=32 StartY=5.34387 StartZ=0 EndX=32 EndY=28.0326 EndZ=0
    g18: ArcOfCircle CenterX=44.5 CenterY=14.5 CenterZ=0 NormalX=0 NormalY=0 NormalZ=1 AngleXU=0 Radius=7.1 StartAngle=2.06504 EndAngle=3.98195
    g19: ArcOfCircle CenterX=38.4285 CenterY=7.72158 CenterZ=0 NormalX=0 NormalY=0 NormalZ=1 AngleXU=0 Radius=2 StartAngle=5.20513 EndAngle=7.12354
    g20: ArcOfCircle CenterX=40.1833 CenterY=22.511 CenterZ=0 NormalX=0 NormalY=0 NormalZ=1 AngleXU=0 Radius=2 StartAngle=5.20663 EndAngle=7.12505
    g21: ArcOfCircle CenterX=34 CenterY=28.0326 CenterZ=0 NormalX=0 NormalY=0 NormalZ=1 AngleXU=0 Radius=2 StartAngle=0.841863 EndAngle=3.14159
    g22: ArcOfCircle CenterX=34 CenterY=5.34387 CenterZ=0 NormalX=0 NormalY=0 NormalZ=1 AngleXU=0 Radius=2 StartAngle=3.14159 EndAngle=5.20513
    g23: LineSegment StartX=34.9461 StartY=3.58178 StartZ=0 EndX=39.3746 EndY=5.9595 EndZ=0
    g24: LineSegment StartX=35.3321 StartY=29.5244 StartZ=0 EndX=41.5154 EndY=24.0027 EndZ=0
    g25: LineSegment [constr] StartX=32 StartY=2 StartZ=0 EndX=34.9461 EndY=3.58178 EndZ=0
    g26: LineSegment [constr] StartX=32 StartY=32.5 StartZ=0 EndX=35.3321 EndY=29.5244 EndZ=0
    g27: LineSegment [constr] StartX=32 StartY=2 StartZ=0 EndX=12 EndY=2 EndZ=0
    g28: LineSegment [constr] StartX=12 StartY=14.5 StartZ=0 EndX=12 EndY=2 EndZ=0
    g29: LineSegment [constr] StartX=12 StartY=2 StartZ=0 EndX=12 EndY=6.0982e-12 EndZ=0
  constraints (73):
    c: Coincident(g2,g1)
    c: Coincident(g3,g1)
    c: Coincident(g3,g0)
    c: Coincident(g4,g0)
    c: Coincident(g5,g0)
    c: PointOnObject(g29,g2)
    c: Coincident(g5,g28)
    c: Vertical(g5)
    c: Distance(g6) = 32.5
    c: Coincident(g6,g5)
    c: Horizontal(g6)
    c: Diameter(g7) = 4.2
    c: Coincident(g7,g6)
    c: Coincident(g8,g6)
    c: Tangent(g10,g2) = -1.5708
    c: Tangent(g10,g9) = -1.5708
    c: Tangent(g9,g8) = -1.5708
    c: Tangent(g12,g4) = 1.5708
    c: Tangent(g12,g11) = 1.5708
    c: Tangent(g11,g8) = 1.5708
    c: Coincident(g13,g6)
    c: PointOnObject(g14,g8)
    c: Coincident(g13,g14)
    c: Horizontal(g13)
    c: Horizontal(g14)
    c: PointOnObject(g13,g7)
    c: Coincident(g15,g12)
    c: Vertical(g15)
    c: Vertical(g16)
    c: Coincident(g17,g16)
    c: Coincident(g17,g15)
    c: Coincident(g18,g6)
    c: Equal(g18,g8)
    c: Coincident(g21,g15)
    c: Coincident(g22,g16)
    c: Tangent(g24,g20) = 1.5708
    c: Tangent(g19,g18) = 1.5708
    c: Tangent(g23,g19) = -1.5708
    c: Tangent(g23,g22) = -1.5708
    c: Tangent(g22,g17)
    c: Tangent(g21,g17)
    c: Tangent(g24,g21) = 1.5708
    c: Parallel(g24,g11)
    c: Parallel(g23,g9)
    c: Coincident(g25,g16)
    c: Coincident(g25,g22)
    c: Coincident(g26,g12)
    c: Tangent(g26,g21) = 1.5708
    c: Tangent(g20,g18) = 1.5708
    c: Parallel(g25,g9)
    c: Equal(g12,g10)
    c: Radius(g22) = 2
    c: Equal(g22,g19)
    c: Equal(g19,g20)
    c: Equal(g20,g21)
    c: Equal(g1,g-3)
    c: Coincident(g-3,g1)
    c: Equal(g0,g-4)
    c: Coincident(g0,g-4)
    c: Coincident(g4,g-5)
    c: Coincident(g12,g-5)
    c: Coincident(g-6,g2)
    c: Coincident(g10,g16)
    c: Coincident(g27,g10)
    c: Horizontal(g27)
    c: Coincident(g28,g29)
    c: Vertical(g28)
    c: Vertical(g29)
    c: Coincident(g28,g27)
    c: DistanceY(g28,g28) = 12.5
    c: Coincident(g0,g-4)
    c: DistanceX(g14,g14) = 5
    c: Coincident(g1,g-3)
FEATURE [PartDesign::Pad] Pad016  label="P-Power Supply Bracket - High - raw001"
  BaseFeature = -> Pocket007
  Direction = (0,0,1)
  Length = 2.4
  Length2 = 10
  Profile = -> Sketch032
  ReferenceAxis = -> Sketch032 [N_Axis]
  Refine = true
  Suppressed = false
  Type = 0
FEATURE [Sketcher::SketchObject] Sketch033  label="Sk-Power Supply Bracket - High - Mounting Screw Hole001"
  ArcFitTolerance = 1e-06
  AttachmentSupport = -> [Pad016]
  ExternalGeometry = -> [Pad016]
  FullyConstrained = true
  MakeInternals = false
  MapMode = 5
  Placement = pos=(0,0,117.9) rot=(0,0,1;0rad)
  sketch-geometry (1):
    g0: Circle CenterX=44.5 CenterY=14.5 CenterZ=0 NormalX=0 NormalY=0 NormalZ=1 AngleXU=0 Radius=2.1
  constraints (2):
    c: Coincident(g0,g-3)
    c: Equal(g0,g-3)
FEATURE [PartDesign::Hole] Hole006  label="P-Power Supply Bracket - High - LED Bottom"
  BaseFeature = -> Pad016
  CustomThreadClearance = 0
  Depth = 25
  DepthType = 0
  Diameter = 4
  DrillForDepth = false
  DrillPoint = 1
  DrillPointAngle = 118
  HoleCutCountersinkAngle = 90
  HoleCutCustomValues = false
  HoleCutDepth = 0
  HoleCutDiameter = 8.2
  HoleCutType = 2
  ModelThread = false
  Profile = -> Sketch033
  Refine = true
  Suppressed = false
  Tapered = false
  TaperedAngle = 90
  ThreadClass = 0
  ThreadDepth = 25
  ThreadDepthType = 0
  ThreadDirection = 0
  ThreadFit = 0
  ThreadSize = 0
  ThreadType = 0
  Threaded = false
  UseCustomThreadClearance = false
FEATURE [PartDesign::Body] Body006  label="B-Power Supply Bracket - High - LED Bottom"
  AllowCompound = false
  Group = -> [Sketch029,Pad015,Sketch030,Pocket006,Sketch031,Pocket007,Sketch032,Pad016,Sketch033,Hole006]
  Origin = -> Origin006
  Placement = pos=(0,-62.8,0) rot=(0,0,1;0rad)
  Tip = -> Hole006
FEATURE [Sketcher::SketchObject] Sketch034  label="Sk-Power Supply Bracket - High - Mounting Screw Hole"
  ArcFitTolerance = 1e-06
  AttachmentSupport = -> [Pad014]
  ExternalGeometry = -> [Pad014]
  FullyConstrained = true
  MakeInternals = false
  MapMode = 5
  Placement = pos=(0,0,-2.5) rot=(1,0,0;3.14159rad)
  sketch-geometry (1):
    g0: Circle CenterX=44.5 CenterY=-14.5 CenterZ=0 NormalX=0 NormalY=0 NormalZ=1 AngleXU=0 Radius=2.1
  constraints (2):
    c: Coincident(g0,g-3)
    c: Equal(g0,g-3)
FEATURE [PartDesign::Hole] Hole007  label="P-Power Supply Bracket - High - LED Top"
  BaseFeature = -> Pad014
  CustomThreadClearance = 0
  Depth = 25
  DepthType = 0
  Diameter = 4
  DrillForDepth = false
  DrillPoint = 1
  DrillPointAngle = 118
  HoleCutCountersinkAngle = 90
  HoleCutCustomValues = false
  HoleCutDepth = 0
  HoleCutDiameter = 8.2
  HoleCutType = 2
  ModelThread = false
  Profile = -> Sketch034
  Refine = true
  Suppressed = false
  Tapered = false
  TaperedAngle = 90
  ThreadClass = 0
  ThreadDepth = 25
  ThreadDepthType = 0
  ThreadDirection = 0
  ThreadFit = 0
  ThreadSize = 0
  ThreadType = 0
  Threaded = false
  UseCustomThreadClearance = false
FEATURE [PartDesign::Body] Body005  label="B-Power Supply Bracket - High - LED Top"
  AllowCompound = false
  Group = -> [Sketch023,Pad013,Sketch026,Pocket004,Sketch027,Pocket005,Sketch028,Pad014,Sketch034,Hole007]
  Origin = -> Origin005
  Tip = -> Hole007
FEATURE [Mesh::Feature] Mesh003  label="M-Power Supply Mounting Brace - High"
FEATURE [Mesh::Feature] Mesh004  label="M-Power Supply Bracket - High - LED Top"
FEATURE [Mesh::Feature] Mesh005  label="M-Power Supply Bracket - High - LED Bottom"
FEATURE [Sketcher::SketchObject] Sketch035  label="Sk-PsMb-ScrewExtender_2mm"
  ArcFitTolerance = 1e-06
  AttachmentSupport = -> [Fillet]
  ExternalGeometry = -> [Fillet]
  FullyConstrained = true
  MakeInternals = false
  MapMode = 5
  Placement = pos=(37,0,0) rot=(0.57735,0.57735,0.57735;2.0944rad)
  sketch-geometry (26):
    g0: LineSegment StartX=0 StartY=91 StartZ=0 EndX=0 EndY=80 EndZ=0
    g1: LineSegment StartX=2 StartY=78 StartZ=0 EndX=18 EndY=78 EndZ=0
    g2: LineSegment StartX=20 StartY=80 StartZ=0 EndX=20 EndY=91 EndZ=0
    g3: LineSegment StartX=18 StartY=93 StartZ=0 EndX=2 EndY=93 EndZ=0
    g4: ArcOfCircle CenterX=2 CenterY=91 CenterZ=0 NormalX=0 NormalY=0 NormalZ=1 AngleXU=0 Radius=2 StartAngle=1.5708 EndAngle=3.14159
    g5: GeomPoint [constr] X=-1e-16 Y=93 Z=0
    g6: ArcOfCircle CenterX=18 CenterY=91 CenterZ=0 NormalX=0 NormalY=0 NormalZ=1 AngleXU=0 Radius=2 StartAngle=-9e-16 EndAngle=1.5708
    g7: GeomPoint [constr] X=20 Y=93 Z=0
    g8: ArcOfCircle CenterX=18 CenterY=80 CenterZ=0 NormalX=0 NormalY=0 NormalZ=1 AngleXU=0 Radius=2 StartAngle=4.71239 EndAngle=6.28319
    g9: GeomPoint [constr] X=20 Y=78 Z=0
    g10: ArcOfCircle CenterX=2 CenterY=80 CenterZ=0 NormalX=0 NormalY=0 NormalZ=1 AngleXU=0 Radius=2 StartAngle=3.14159 EndAngle=4.71239
    g11: GeomPoint [constr] X=-1e-16 Y=78 Z=0
    g12: LineSegment [constr] StartX=10 StartY=85.5 StartZ=0 EndX=10 EndY=93 EndZ=0
    g13: LineSegment [constr] StartX=10 StartY=85.5 StartZ=0 EndX=10 EndY=78 EndZ=0
    g14: LineSegment StartX=0 StartY=41 StartZ=0 EndX=0 EndY=30 EndZ=0
    g15: LineSegment StartX=2 StartY=28 StartZ=0 EndX=18 EndY=28 EndZ=0
    g16: LineSegment StartX=20 StartY=30 StartZ=0 EndX=20 EndY=41 EndZ=0
    g17: LineSegment StartX=18 StartY=43 StartZ=0 EndX=2 EndY=43 EndZ=0
    g18: ArcOfCircle CenterX=2 CenterY=41 CenterZ=0 NormalX=0 NormalY=0 NormalZ=1 AngleXU=0 Radius=2 StartAngle=1.5708 EndAngle=3.14159
    g19: ArcOfCircle CenterX=2 CenterY=30 CenterZ=0 NormalX=0 NormalY=0 NormalZ=1 AngleXU=0 Radius=2 StartAngle=3.14159 EndAngle=4.71239
    g20: ArcOfCircle CenterX=18 CenterY=30 CenterZ=0 NormalX=0 NormalY=0 NormalZ=1 AngleXU=0 Radius=2 StartAngle=4.71239 EndAngle=6.28319
    g21: ArcOfCircle CenterX=18 CenterY=41 CenterZ=0 NormalX=0 NormalY=0 NormalZ=1 AngleXU=0 Radius=2 StartAngle=0 EndAngle=1.5708
    g22: GeomPoint [constr] X=-1e-16 Y=43 Z=0
    g23: GeomPoint [constr] X=20 Y=28 Z=0
    g24: LineSegment [constr] StartX=10 StartY=35.5 StartZ=0 EndX=10 EndY=43 EndZ=0
    g25: LineSegment [constr] StartX=10 StartY=35.5 StartZ=0 EndX=10 EndY=28 EndZ=0
  constraints (60):
    c: Vertical(g0)
    c: Vertical(g2)
    c: Horizontal(g1)
    c: Horizontal(g3)
    c: PointOnObject(g9,g-6)
    c: PointOnObject(g5,g0)
    c: PointOnObject(g5,g3)
    c: Tangent(g0,g4) = -1.5708
    c: Tangent(g3,g4) = -1.5708
    c: PointOnObject(g7,g3)
    c: PointOnObject(g7,g2)
    c: Tangent(g3,g6) = -1.5708
    c: Tangent(g2,g6) = -1.5708
    c: PointOnObject(g9,g2)
    c: PointOnObject(g9,g1)
    c: Tangent(g2,g8) = -1.5708
    c: Tangent(g1,g8) = -1.5708
    c: PointOnObject(g11,g1)
    c: PointOnObject(g11,g0)
    c: Tangent(g1,g10) = -1.5708
    c: Tangent(g0,g10) = -1.5708
    c: Coincident(g0,g-5)
    c: Coincident(g3,g-7)
    c: Equal(g6,g8)
    c: Equal(g8,g10)
    c: Coincident(g12,g-3)
    c: Symmetric(g3,g3,g12)
    c: Coincident(g13,g12)
    c: Symmetric(g1,g1,g13)
    c: Equal(g12,g13)
    c: Tangent(g14,g18) = -1.5708
    c: Tangent(g14,g19) = -1.5708
    c: Tangent(g15,g19) = -1.5708
    c: Tangent(g15,g20) = -1.5708
    c: Tangent(g16,g20) = -1.5708
    c: Tangent(g16,g21) = -1.5708
    c: Tangent(g17,g21) = -1.5708
    c: Tangent(g17,g18) = -1.5708
    c: Vertical(g14)
    c: Vertical(g16)
    c: Horizontal(g15)
    c: Horizontal(g17)
    c: Equal(g18,g19)
    c: Equal(g19,g20)
    c: Equal(g20,g21)
    c: PointOnObject(g22,g14)
    c: PointOnObject(g22,g17)
    c: PointOnObject(g23,g15)
    c: PointOnObject(g23,g16)
    c: Equal(g18,g10)
    c: PointOnObject(g14,g-5)
    c: PointOnObject(g16,g-6)
    c: Coincident(g24,g-4)
    c: PointOnObject(g24,g17)
    c: Coincident(g25,g24)
    c: PointOnObject(g25,g15)
    c: Vertical(g25)
    c: Vertical(g24)
    c: Equal(g25,g24)
    c: Equal(g24,g13)
FEATURE [PartDesign::Pad] Pad017  label="P-PsMb-ScrewExtender_2mm raw"
  BaseFeature = -> Fillet
  Direction = (1,0,0)
  Length = 4
  Length2 = 10
  Midplane = true
  Profile = -> Sketch035
  ReferenceAxis = -> Sketch035 [N_Axis]
  Refine = true
  Suppressed = false
  Type = 0
FEATURE [Sketcher::SketchObject] Sketch036  label="Sk-PsMb-ScrewExtender_2mm_Drilling"
  ArcFitTolerance = 1e-06
  AttachmentSupport = -> [Pad017]
  ExternalGeometry = -> [Pad017]
  FullyConstrained = true
  MakeInternals = false
  MapMode = 5
  Placement = pos=(39,0,0) rot=(0.57735,0.57735,0.57735;2.0944rad)
  sketch-geometry (2):
    g0: Circle CenterX=10 CenterY=85.5 CenterZ=0 NormalX=0 NormalY=0 NormalZ=1 AngleXU=0 Radius=2.1
    g1: Circle CenterX=10 CenterY=35.5 CenterZ=0 NormalX=0 NormalY=0 NormalZ=1 AngleXU=0 Radius=2.1
  constraints (4):
    c: Coincident(g0,g-3)
    c: Equal(g0,g-3)
    c: Coincident(g1,g-4)
    c: Equal(g1,g-4)
FEATURE [PartDesign::Hole] Hole008  label="P-PsMb-ScrewExtender_2mm drilled"
  BaseFeature = -> Pad017
  CustomThreadClearance = 0
  Depth = 25
  DepthType = 0
  Diameter = 4.2
  DrillForDepth = false
  DrillPoint = 1
  DrillPointAngle = 118
  HoleCutCountersinkAngle = 90
  HoleCutCustomValues = false
  HoleCutDepth = 0
  HoleCutDiameter = 8.2
  HoleCutType = 2
  ModelThread = false
  Profile = -> Sketch036
  Refine = true
  Suppressed = false
  Tapered = false
  TaperedAngle = 90
  ThreadClass = 0
  ThreadDepth = 25
  ThreadDepthType = 0
  ThreadDirection = 0
  ThreadFit = 0
  ThreadSize = 0
  ThreadType = 0
  Threaded = false
  UseCustomThreadClearance = false
FEATURE [PartDesign::Fillet] Fillet002  label="P-PsMb with Screwextender"
  Base = -> Hole008 [Edge102,Edge88]
  BaseFeature = -> Hole008
  Radius = 0.8
  Refine = true
  SupportTransform = false
  Suppressed = false
  UseAllEdges = false
FEATURE [PartDesign::Body] Body003  label="B-Power Supply Mounting Brace - High"
  AllowCompound = false
  Group = -> [Sketch013,Pad007,Sketch014,Pad008,Sketch015,Pad009,Sketch016,Hole004,Sketch017,Pocket002,Chamfer,Fillet,Sketch035,Pad017,Sketch036,Hole008,Fillet002]
  Origin = -> Origin003
  Placement = pos=(-104.9,0,0) rot=(0,0,1;0rad)
  Tip = -> Fillet002
FEATURE [Mesh::Feature] Mesh006  label="M-Power Supply Mounting Brace - High w. Screwextender"
FEATURE [Sketcher::SketchObject] Sketch037
  ArcFitTolerance = 1e-06
  AttachmentSupport = -> [XY_Plane007]
  FullyConstrained = true
  MakeInternals = false
  MapMode = 5
  sketch-geometry (2):
    g0: Circle CenterX=0 CenterY=0 CenterZ=0 NormalX=0 NormalY=0 NormalZ=1 AngleXU=0 Radius=6
    g1: Circle CenterX=0 CenterY=0 CenterZ=0 NormalX=0 NormalY=0 NormalZ=1 AngleXU=0 Radius=2.1
  constraints (4):
    c: Diameter(g0) = 12
    c: Coincident(g0,g-1)
    c: Diameter(g1) = 4.2
    c: Coincident(g1,g0)
FEATURE [PartDesign::Pad] Pad018  label="P-Screwextender_M4_2mm - Base"
  Direction = (0,0,1)
  Length = 2
  Length2 = 10
  Profile = -> Sketch037
  ReferenceAxis = -> Sketch037 [N_Axis]
  Refine = true
  Suppressed = false
  Type = 0
FEATURE [Sketcher::SketchObject] Sketch038  label="B-Screwextender_M4_2mm - Hole btm"
  ArcFitTolerance = 1e-06
  AttachmentSupport = -> [Pad018]
  ExternalGeometry = -> [Pad018]
  FullyConstrained = true
  MakeInternals = false
  MapMode = 5
  Placement = pos=(0,0,0) rot=(1,0,0;3.14159rad)
  sketch-geometry (1):
    g0: Circle CenterX=0 CenterY=0 CenterZ=0 NormalX=0 NormalY=0 NormalZ=1 AngleXU=0 Radius=2.1
  constraints (2):
    c: Coincident(g0,g-1)
    c: Equal(g-3,g0)
FEATURE [PartDesign::Plane] DatumPlane
  AttachmentSupport = -> [Pad018]
  Length = 60
  MapMode = 12
  Placement = pos=(0,0,2) rot=(1,0,0;1.5708rad)
  ResizeMode = 0
  Width = 60
FEATURE [Sketcher::SketchObject] Sketch039  label="B-Screwextender_M4_2mm - Cone Profile"
  ArcFitTolerance = 1e-06
  AttachmentSupport = -> [DatumPlane]
  ExternalGeometry = -> [Pad018]
  FullyConstrained = true
  MakeInternals = false
  MapMode = 5
  Placement = pos=(0,0,2) rot=(1,0,0;1.5708rad)
  sketch-geometry (3):
    g0: LineSegment StartX=2.1 StartY=1.9 StartZ=0 EndX=2.1 EndY=0 EndZ=0
    g1: LineSegment StartX=4 StartY=0 StartZ=0 EndX=2.1 EndY=1.9 EndZ=0
    g2: LineSegment StartX=2.1 StartY=0 StartZ=0 EndX=4 EndY=0 EndZ=0
  constraints (9):
    c: PointOnObject(g1,g-1)
    c: Coincident(g1,g0)
    c: Coincident(g2,g1)
    c: DistanceX(g2,g2) = 1.9
    c: Angle(g1,g2) = 0.785398
    c: Coincident(g0,g2)
    c: Vertical(g0)
    c: Horizontal(g2)
    c: PointOnObject(g-3,g0)
FEATURE [PartDesign::Revolution] Revolution  label="P-Screwextender_M4_2mm - Cone"
  Angle = 360
  Angle2 = 60
  Axis = (0,2e-16,1)
  Base = (0,0,2)
  BaseFeature = -> Pad018
  Profile = -> Sketch039
  ReferenceAxis = -> Sketch039 [V_Axis]
  Refine = true
  Reversed = true
  Suppressed = false
  Type = 0
FEATURE [PartDesign::Hole] Hole009  label="P-Screwextender_M4_2mm"
  BaseFeature = -> Revolution
  CustomThreadClearance = 0
  Depth = 25
  DepthType = 0
  Diameter = 4.2
  DrillForDepth = false
  DrillPoint = 1
  DrillPointAngle = 118
  HoleCutCountersinkAngle = 90
  HoleCutCustomValues = false
  HoleCutDepth = 0
  HoleCutDiameter = 8.2
  HoleCutType = 2
  ModelThread = false
  Profile = -> Sketch038
  Refine = true
  Suppressed = false
  Tapered = false
  TaperedAngle = 90
  ThreadClass = 0
  ThreadDepth = 25
  ThreadDepthType = 0
  ThreadDirection = 0
  ThreadFit = 0
  ThreadSize = 0
  ThreadType = 0
  Threaded = false
  UseCustomThreadClearance = false
FEATURE [PartDesign::Body] Body007  label="B-Screwextender_M4_2mm"
  AllowCompound = false
  Group = -> [Sketch037,Pad018,Sketch038,DatumPlane,Sketch039,Revolution,Hole009]
  Origin = -> Origin007
  Tip = -> Hole009
FEATURE [Mesh::Feature] Mesh007  label="M-Screwextender_M4_2mm"
